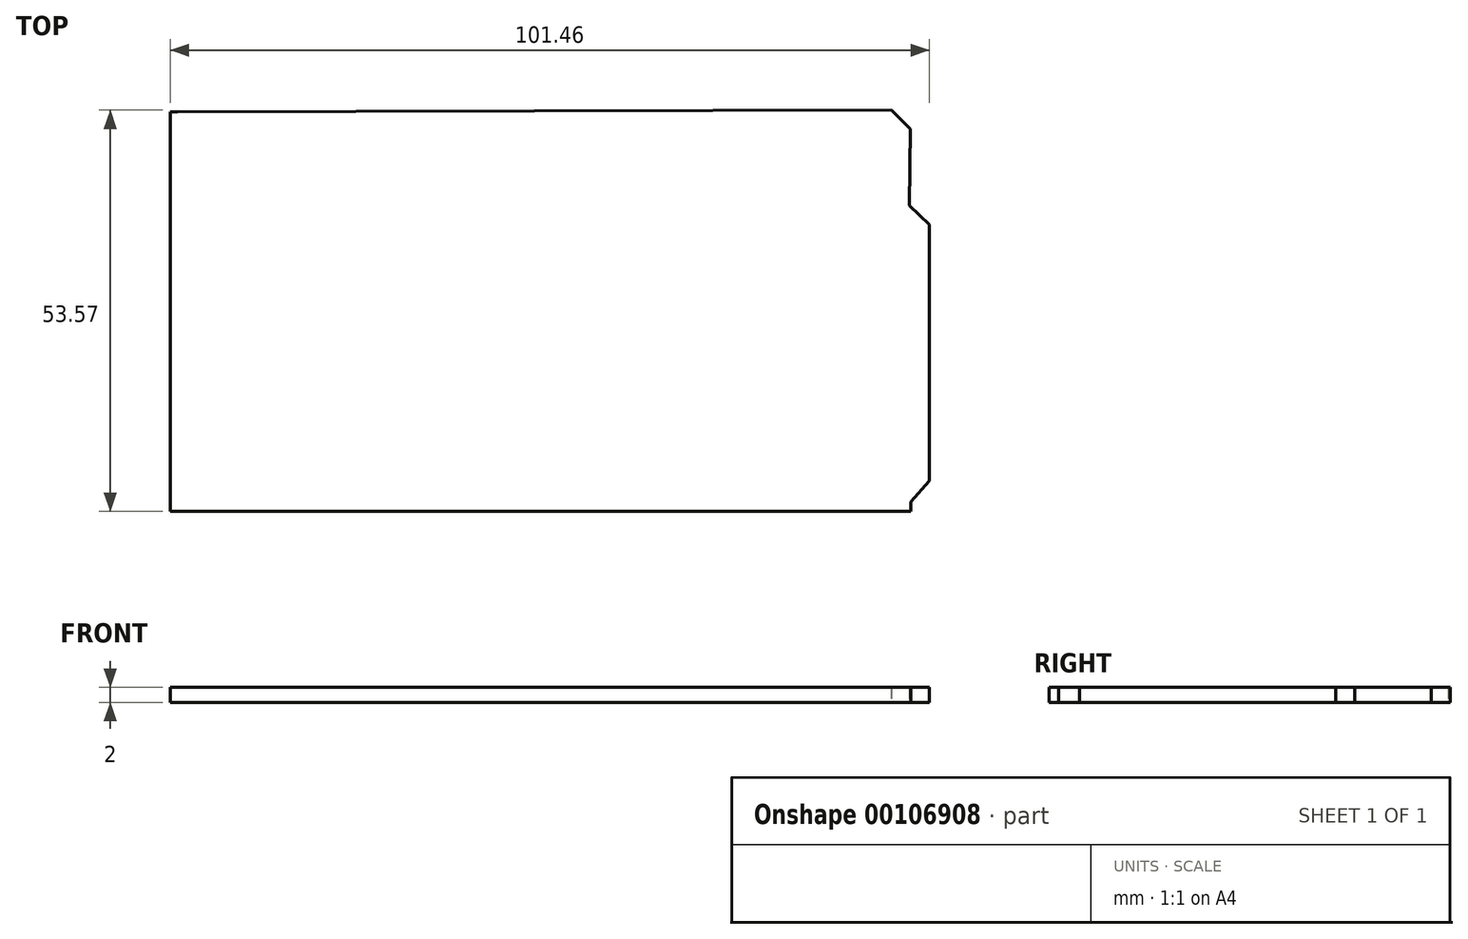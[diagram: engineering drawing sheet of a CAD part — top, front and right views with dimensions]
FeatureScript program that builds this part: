
annotation { "Feature Type Name" : "Feature", "Feature Type Description" : "" }
export const myFeature = defineFeature(function(context is Context, id is Id, definition is map)
    precondition{}
    {
        {
            var Q0;
            Q0=qCreatedBy(makeId("Top.planeOp"),FACE);
            var sketch = newSketch(context, id + "F0", { "sketchPlane" : qUnion([Q0])});
            skLineSegment(sketch, "E0", {"start": v(-9.69, 13.35) * mm, "end": v(-9.69, 13.4) * mm});
            skLineSegment(sketch, "E1", {"start": v(-9.69, 13.4) * mm, "end": v(-9.7, 13.46) * mm});
            skLineSegment(sketch, "E2", {"start": v(-9.7, 13.46) * mm, "end": v(-9.7, 13.51) * mm});
            skLineSegment(sketch, "E3", {"start": v(-9.7, 13.51) * mm, "end": v(-9.7, 13.57) * mm});
            skLineSegment(sketch, "E4", {"start": v(-9.7, 13.57) * mm, "end": v(-9.71, 13.63) * mm});
            skLineSegment(sketch, "E5", {"start": v(-9.71, 13.63) * mm, "end": v(-9.72, 13.68) * mm});
            skLineSegment(sketch, "E6", {"start": v(-9.72, 13.68) * mm, "end": v(-9.73, 13.73) * mm});
            skLineSegment(sketch, "E7", {"start": v(-9.73, 13.73) * mm, "end": v(-9.75, 13.79) * mm});
            skLineSegment(sketch, "E8", {"start": v(-9.75, 13.79) * mm, "end": v(-9.76, 13.84) * mm});
            skLineSegment(sketch, "E9", {"start": v(-9.76, 13.84) * mm, "end": v(-9.78, 13.9) * mm});
            skLineSegment(sketch, "E10", {"start": v(-9.78, 13.9) * mm, "end": v(-9.8, 13.95) * mm});
            skLineSegment(sketch, "E11", {"start": v(-9.8, 13.95) * mm, "end": v(-9.82, 14) * mm});
            skLineSegment(sketch, "E12", {"start": v(-9.82, 14) * mm, "end": v(-9.85, 14.05) * mm});
            skLineSegment(sketch, "E13", {"start": v(-9.85, 14.05) * mm, "end": v(-9.87, 14.1) * mm});
            skLineSegment(sketch, "E14", {"start": v(-9.87, 14.1) * mm, "end": v(-9.9, 14.15) * mm});
            skLineSegment(sketch, "E15", {"start": v(-9.9, 14.15) * mm, "end": v(-9.93, 14.2) * mm});
            skLineSegment(sketch, "E16", {"start": v(-9.93, 14.2) * mm, "end": v(-9.96, 14.24) * mm});
            skLineSegment(sketch, "E17", {"start": v(-9.96, 14.24) * mm, "end": v(-9.99, 14.29) * mm});
            skLineSegment(sketch, "E18", {"start": v(-9.99, 14.29) * mm, "end": v(-10.02, 14.33) * mm});
            skLineSegment(sketch, "E19", {"start": v(-10.02, 14.33) * mm, "end": v(-10.06, 14.38) * mm});
            skLineSegment(sketch, "E20", {"start": v(-10.06, 14.38) * mm, "end": v(-10.1, 14.42) * mm});
            skLineSegment(sketch, "E21", {"start": v(-10.1, 14.42) * mm, "end": v(-10.13, 14.46) * mm});
            skLineSegment(sketch, "E22", {"start": v(-10.13, 14.46) * mm, "end": v(-10.17, 14.5) * mm});
            skLineSegment(sketch, "E23", {"start": v(-10.17, 14.5) * mm, "end": v(-10.21, 14.54) * mm});
            skLineSegment(sketch, "E24", {"start": v(-10.21, 14.54) * mm, "end": v(-10.25, 14.57) * mm});
            skLineSegment(sketch, "E25", {"start": v(-10.25, 14.57) * mm, "end": v(-10.3, 14.6) * mm});
            skLineSegment(sketch, "E26", {"start": v(-10.3, 14.6) * mm, "end": v(-10.34, 14.64) * mm});
            skLineSegment(sketch, "E27", {"start": v(-10.34, 14.64) * mm, "end": v(-10.39, 14.67) * mm});
            skLineSegment(sketch, "E28", {"start": v(-10.39, 14.67) * mm, "end": v(-10.43, 14.7) * mm});
            skLineSegment(sketch, "E29", {"start": v(-10.43, 14.7) * mm, "end": v(-10.48, 14.73) * mm});
            skLineSegment(sketch, "E30", {"start": v(-10.48, 14.73) * mm, "end": v(-10.53, 14.76) * mm});
            skLineSegment(sketch, "E31", {"start": v(-10.53, 14.76) * mm, "end": v(-10.58, 14.79) * mm});
            skLineSegment(sketch, "E32", {"start": v(-10.58, 14.79) * mm, "end": v(-10.63, 14.81) * mm});
            skLineSegment(sketch, "E33", {"start": v(-10.63, 14.81) * mm, "end": v(-10.68, 14.83) * mm});
            skLineSegment(sketch, "E34", {"start": v(-10.68, 14.83) * mm, "end": v(-10.73, 14.85) * mm});
            skLineSegment(sketch, "E35", {"start": v(-10.73, 14.85) * mm, "end": v(-10.78, 14.87) * mm});
            skLineSegment(sketch, "E36", {"start": v(-10.78, 14.87) * mm, "end": v(-10.84, 14.89) * mm});
            skLineSegment(sketch, "E37", {"start": v(-10.84, 14.89) * mm, "end": v(-10.9, 14.9) * mm});
            skLineSegment(sketch, "E38", {"start": v(-10.9, 14.9) * mm, "end": v(-10.95, 14.92) * mm});
            skLineSegment(sketch, "E39", {"start": v(-10.95, 14.92) * mm, "end": v(-11, 14.93) * mm});
            skLineSegment(sketch, "E40", {"start": v(-11, 14.93) * mm, "end": v(-11.05, 14.94) * mm});
            skLineSegment(sketch, "E41", {"start": v(-11.05, 14.94) * mm, "end": v(-11.1, 14.95) * mm});
            skLineSegment(sketch, "E42", {"start": v(-11.1, 14.95) * mm, "end": v(-11.17, 14.95) * mm});
            skLineSegment(sketch, "E43", {"start": v(-11.17, 14.95) * mm, "end": v(-11.22, 14.95) * mm});
            skLineSegment(sketch, "E44", {"start": v(-11.22, 14.95) * mm, "end": v(-11.28, 14.96) * mm});
            skLineSegment(sketch, "E45", {"start": v(-11.28, 14.96) * mm, "end": v(-11.33, 14.96) * mm});
            skLineSegment(sketch, "E46", {"start": v(-11.33, 14.96) * mm, "end": v(-11.39, 14.95) * mm});
            skLineSegment(sketch, "E47", {"start": v(-11.39, 14.95) * mm, "end": v(-11.44, 14.95) * mm});
            skLineSegment(sketch, "E48", {"start": v(-11.44, 14.95) * mm, "end": v(-11.5, 14.94) * mm});
            skLineSegment(sketch, "E49", {"start": v(-11.5, 14.94) * mm, "end": v(-11.55, 14.94) * mm});
            skLineSegment(sketch, "E50", {"start": v(-11.55, 14.94) * mm, "end": v(-11.6, 14.93) * mm});
            skLineSegment(sketch, "E51", {"start": v(-11.6, 14.93) * mm, "end": v(-11.66, 14.91) * mm});
            skLineSegment(sketch, "E52", {"start": v(-11.66, 14.91) * mm, "end": v(-11.72, 14.9) * mm});
            skLineSegment(sketch, "E53", {"start": v(-11.72, 14.9) * mm, "end": v(-11.77, 14.88) * mm});
            skLineSegment(sketch, "E54", {"start": v(-11.77, 14.88) * mm, "end": v(-11.82, 14.87) * mm});
            skLineSegment(sketch, "E55", {"start": v(-11.82, 14.87) * mm, "end": v(-11.88, 14.85) * mm});
            skLineSegment(sketch, "E56", {"start": v(-11.88, 14.85) * mm, "end": v(-11.93, 14.83) * mm});
            skLineSegment(sketch, "E57", {"start": v(-11.93, 14.83) * mm, "end": v(-11.98, 14.8) * mm});
            skLineSegment(sketch, "E58", {"start": v(-11.98, 14.8) * mm, "end": v(-12.03, 14.78) * mm});
            skLineSegment(sketch, "E59", {"start": v(-12.03, 14.78) * mm, "end": v(-12.08, 14.75) * mm});
            skLineSegment(sketch, "E60", {"start": v(-12.08, 14.75) * mm, "end": v(-12.13, 14.72) * mm});
            skLineSegment(sketch, "E61", {"start": v(-12.13, 14.72) * mm, "end": v(-12.17, 14.7) * mm});
            skLineSegment(sketch, "E62", {"start": v(-12.17, 14.7) * mm, "end": v(-12.22, 14.66) * mm});
            skLineSegment(sketch, "E63", {"start": v(-12.22, 14.66) * mm, "end": v(-12.26, 14.63) * mm});
            skLineSegment(sketch, "E64", {"start": v(-12.26, 14.63) * mm, "end": v(-12.3, 14.6) * mm});
            skLineSegment(sketch, "E65", {"start": v(-12.3, 14.6) * mm, "end": v(-12.35, 14.56) * mm});
            skLineSegment(sketch, "E66", {"start": v(-12.35, 14.56) * mm, "end": v(-12.4, 14.52) * mm});
            skLineSegment(sketch, "E67", {"start": v(-12.4, 14.52) * mm, "end": v(-12.43, 14.49) * mm});
            skLineSegment(sketch, "E68", {"start": v(-12.43, 14.49) * mm, "end": v(-12.47, 14.45) * mm});
            skLineSegment(sketch, "E69", {"start": v(-12.47, 14.45) * mm, "end": v(-12.5, 14.4) * mm});
            skLineSegment(sketch, "E70", {"start": v(-12.5, 14.4) * mm, "end": v(-12.54, 14.36) * mm});
            skLineSegment(sketch, "E71", {"start": v(-12.54, 14.36) * mm, "end": v(-12.58, 14.32) * mm});
            skLineSegment(sketch, "E72", {"start": v(-12.58, 14.32) * mm, "end": v(-12.61, 14.27) * mm});
            skLineSegment(sketch, "E73", {"start": v(-12.61, 14.27) * mm, "end": v(-12.64, 14.23) * mm});
            skLineSegment(sketch, "E74", {"start": v(-12.64, 14.23) * mm, "end": v(-12.67, 14.18) * mm});
            skLineSegment(sketch, "E75", {"start": v(-12.67, 14.18) * mm, "end": v(-12.7, 14.13) * mm});
            skLineSegment(sketch, "E76", {"start": v(-12.7, 14.13) * mm, "end": v(-12.73, 14.08) * mm});
            skLineSegment(sketch, "E77", {"start": v(-12.73, 14.08) * mm, "end": v(-12.75, 14.03) * mm});
            skLineSegment(sketch, "E78", {"start": v(-12.75, 14.03) * mm, "end": v(-12.77, 13.98) * mm});
            skLineSegment(sketch, "E79", {"start": v(-12.77, 13.98) * mm, "end": v(-12.8, 13.93) * mm});
            skLineSegment(sketch, "E80", {"start": v(-12.8, 13.93) * mm, "end": v(-12.81, 13.88) * mm});
            skLineSegment(sketch, "E81", {"start": v(-12.81, 13.88) * mm, "end": v(-12.83, 13.82) * mm});
            skLineSegment(sketch, "E82", {"start": v(-12.83, 13.82) * mm, "end": v(-12.85, 13.77) * mm});
            skLineSegment(sketch, "E83", {"start": v(-12.85, 13.77) * mm, "end": v(-12.86, 13.72) * mm});
            skLineSegment(sketch, "E84", {"start": v(-12.86, 13.72) * mm, "end": v(-12.87, 13.66) * mm});
            skLineSegment(sketch, "E85", {"start": v(-12.87, 13.66) * mm, "end": v(-12.88, 13.6) * mm});
            skLineSegment(sketch, "E86", {"start": v(-12.88, 13.6) * mm, "end": v(-12.9, 13.55) * mm});
            skLineSegment(sketch, "E87", {"start": v(-12.9, 13.55) * mm, "end": v(-12.9, 13.5) * mm});
            skLineSegment(sketch, "E88", {"start": v(-12.9, 13.5) * mm, "end": v(-12.9, 13.44) * mm});
            skLineSegment(sketch, "E89", {"start": v(-12.9, 13.44) * mm, "end": v(-12.9, 13.39) * mm});
            skLineSegment(sketch, "E90", {"start": v(-12.9, 13.39) * mm, "end": v(-12.9, 13.33) * mm});
            skLineSegment(sketch, "E91", {"start": v(-12.9, 13.33) * mm, "end": v(-12.9, 13.27) * mm});
            skLineSegment(sketch, "E92", {"start": v(-12.9, 13.27) * mm, "end": v(-12.9, 13.22) * mm});
            skLineSegment(sketch, "E93", {"start": v(-12.9, 13.22) * mm, "end": v(-12.9, 13.16) * mm});
            skLineSegment(sketch, "E94", {"start": v(-12.9, 13.16) * mm, "end": v(-12.89, 13.1) * mm});
            skLineSegment(sketch, "E95", {"start": v(-12.89, 13.1) * mm, "end": v(-12.88, 13.05) * mm});
            skLineSegment(sketch, "E96", {"start": v(-12.88, 13.05) * mm, "end": v(-12.86, 13) * mm});
            skLineSegment(sketch, "E97", {"start": v(-12.86, 13) * mm, "end": v(-12.85, 12.94) * mm});
            skLineSegment(sketch, "E98", {"start": v(-12.85, 12.94) * mm, "end": v(-12.84, 12.9) * mm});
            skLineSegment(sketch, "E99", {"start": v(-12.84, 12.9) * mm, "end": v(-12.82, 12.84) * mm});
            skLineSegment(sketch, "E100", {"start": v(-12.82, 12.84) * mm, "end": v(-12.8, 12.78) * mm});
            skLineSegment(sketch, "E101", {"start": v(-12.8, 12.78) * mm, "end": v(-12.78, 12.73) * mm});
            skLineSegment(sketch, "E102", {"start": v(-12.78, 12.73) * mm, "end": v(-12.76, 12.68) * mm});
            skLineSegment(sketch, "E103", {"start": v(-12.76, 12.68) * mm, "end": v(-12.73, 12.63) * mm});
            skLineSegment(sketch, "E104", {"start": v(-12.73, 12.63) * mm, "end": v(-12.7, 12.58) * mm});
            skLineSegment(sketch, "E105", {"start": v(-12.7, 12.58) * mm, "end": v(-12.68, 12.53) * mm});
            skLineSegment(sketch, "E106", {"start": v(-12.68, 12.53) * mm, "end": v(-12.65, 12.49) * mm});
            skLineSegment(sketch, "E107", {"start": v(-12.65, 12.49) * mm, "end": v(-12.62, 12.44) * mm});
            skLineSegment(sketch, "E108", {"start": v(-12.62, 12.44) * mm, "end": v(-12.59, 12.4) * mm});
            skLineSegment(sketch, "E109", {"start": v(-12.59, 12.4) * mm, "end": v(-12.56, 12.35) * mm});
            skLineSegment(sketch, "E110", {"start": v(-12.56, 12.35) * mm, "end": v(-12.52, 12.3) * mm});
            skLineSegment(sketch, "E111", {"start": v(-12.52, 12.3) * mm, "end": v(-12.48, 12.26) * mm});
            skLineSegment(sketch, "E112", {"start": v(-12.48, 12.26) * mm, "end": v(-12.45, 12.22) * mm});
            skLineSegment(sketch, "E113", {"start": v(-12.45, 12.22) * mm, "end": v(-12.4, 12.18) * mm});
            skLineSegment(sketch, "E114", {"start": v(-12.4, 12.18) * mm, "end": v(-12.36, 12.15) * mm});
            skLineSegment(sketch, "E115", {"start": v(-12.36, 12.15) * mm, "end": v(-12.32, 12.11) * mm});
            skLineSegment(sketch, "E116", {"start": v(-12.32, 12.11) * mm, "end": v(-12.28, 12.08) * mm});
            skLineSegment(sketch, "E117", {"start": v(-12.28, 12.08) * mm, "end": v(-12.23, 12.04) * mm});
            skLineSegment(sketch, "E118", {"start": v(-12.23, 12.04) * mm, "end": v(-12.19, 12.01) * mm});
            skLineSegment(sketch, "E119", {"start": v(-12.19, 12.01) * mm, "end": v(-12.14, 11.98) * mm});
            skLineSegment(sketch, "E120", {"start": v(-12.14, 11.98) * mm, "end": v(-12.1, 11.95) * mm});
            skLineSegment(sketch, "E121", {"start": v(-12.1, 11.95) * mm, "end": v(-12.05, 11.93) * mm});
            skLineSegment(sketch, "E122", {"start": v(-12.05, 11.93) * mm, "end": v(-12, 11.9) * mm});
            skLineSegment(sketch, "E123", {"start": v(-12, 11.9) * mm, "end": v(-11.94, 11.88) * mm});
            skLineSegment(sketch, "E124", {"start": v(-11.94, 11.88) * mm, "end": v(-11.9, 11.86) * mm});
            skLineSegment(sketch, "E125", {"start": v(-11.9, 11.86) * mm, "end": v(-11.84, 11.84) * mm});
            skLineSegment(sketch, "E126", {"start": v(-11.84, 11.84) * mm, "end": v(-11.79, 11.82) * mm});
            skLineSegment(sketch, "E127", {"start": v(-11.79, 11.82) * mm, "end": v(-11.74, 11.8) * mm});
            skLineSegment(sketch, "E128", {"start": v(-11.74, 11.8) * mm, "end": v(-11.68, 11.79) * mm});
            skLineSegment(sketch, "E129", {"start": v(-11.68, 11.79) * mm, "end": v(-11.63, 11.77) * mm});
            skLineSegment(sketch, "E130", {"start": v(-11.63, 11.77) * mm, "end": v(-11.57, 11.76) * mm});
            skLineSegment(sketch, "E131", {"start": v(-11.57, 11.76) * mm, "end": v(-11.52, 11.76) * mm});
            skLineSegment(sketch, "E132", {"start": v(-11.52, 11.76) * mm, "end": v(-11.46, 11.75) * mm});
            skLineSegment(sketch, "E133", {"start": v(-11.46, 11.75) * mm, "end": v(-11.4, 11.74) * mm});
            skLineSegment(sketch, "E134", {"start": v(-11.4, 11.74) * mm, "end": v(-11.35, 11.74) * mm});
            skLineSegment(sketch, "E135", {"start": v(-11.35, 11.74) * mm, "end": v(-11.3, 11.74) * mm});
            skLineSegment(sketch, "E136", {"start": v(-11.3, 11.74) * mm, "end": v(-11.24, 11.74) * mm});
            skLineSegment(sketch, "E137", {"start": v(-11.24, 11.74) * mm, "end": v(-11.18, 11.74) * mm});
            skLineSegment(sketch, "E138", {"start": v(-11.18, 11.74) * mm, "end": v(-11.13, 11.75) * mm});
            skLineSegment(sketch, "E139", {"start": v(-11.13, 11.75) * mm, "end": v(-11.07, 11.76) * mm});
            skLineSegment(sketch, "E140", {"start": v(-11.07, 11.76) * mm, "end": v(-11.02, 11.76) * mm});
            skLineSegment(sketch, "E141", {"start": v(-11.02, 11.76) * mm, "end": v(-10.96, 11.78) * mm});
            skLineSegment(sketch, "E142", {"start": v(-10.96, 11.78) * mm, "end": v(-10.9, 11.79) * mm});
            skLineSegment(sketch, "E143", {"start": v(-10.9, 11.79) * mm, "end": v(-10.85, 11.8) * mm});
            skLineSegment(sketch, "E144", {"start": v(-10.85, 11.8) * mm, "end": v(-10.8, 11.82) * mm});
            skLineSegment(sketch, "E145", {"start": v(-10.8, 11.82) * mm, "end": v(-10.75, 11.84) * mm});
            skLineSegment(sketch, "E146", {"start": v(-10.75, 11.84) * mm, "end": v(-10.7, 11.86) * mm});
            skLineSegment(sketch, "E147", {"start": v(-10.7, 11.86) * mm, "end": v(-10.64, 11.88) * mm});
            skLineSegment(sketch, "E148", {"start": v(-10.64, 11.88) * mm, "end": v(-10.6, 11.9) * mm});
            skLineSegment(sketch, "E149", {"start": v(-10.6, 11.9) * mm, "end": v(-10.54, 11.93) * mm});
            skLineSegment(sketch, "E150", {"start": v(-10.54, 11.93) * mm, "end": v(-10.5, 11.96) * mm});
            skLineSegment(sketch, "E151", {"start": v(-10.5, 11.96) * mm, "end": v(-10.44, 11.98) * mm});
            skLineSegment(sketch, "E152", {"start": v(-10.44, 11.98) * mm, "end": v(-10.4, 12.01) * mm});
            skLineSegment(sketch, "E153", {"start": v(-10.4, 12.01) * mm, "end": v(-10.35, 12.05) * mm});
            skLineSegment(sketch, "E154", {"start": v(-10.35, 12.05) * mm, "end": v(-10.3, 12.08) * mm});
            skLineSegment(sketch, "E155", {"start": v(-10.3, 12.08) * mm, "end": v(-10.26, 12.12) * mm});
            skLineSegment(sketch, "E156", {"start": v(-10.26, 12.12) * mm, "end": v(-10.22, 12.15) * mm});
            skLineSegment(sketch, "E157", {"start": v(-10.22, 12.15) * mm, "end": v(-10.18, 12.2) * mm});
            skLineSegment(sketch, "E158", {"start": v(-10.18, 12.2) * mm, "end": v(-10.14, 12.23) * mm});
            skLineSegment(sketch, "E159", {"start": v(-10.14, 12.23) * mm, "end": v(-10.1, 12.27) * mm});
            skLineSegment(sketch, "E160", {"start": v(-10.1, 12.27) * mm, "end": v(-10.06, 12.31) * mm});
            skLineSegment(sketch, "E161", {"start": v(-10.06, 12.31) * mm, "end": v(-10.03, 12.36) * mm});
            skLineSegment(sketch, "E162", {"start": v(-10.03, 12.36) * mm, "end": v(-10, 12.4) * mm});
            skLineSegment(sketch, "E163", {"start": v(-10, 12.4) * mm, "end": v(-9.96, 12.45) * mm});
            skLineSegment(sketch, "E164", {"start": v(-9.96, 12.45) * mm, "end": v(-9.93, 12.5) * mm});
            skLineSegment(sketch, "E165", {"start": v(-9.93, 12.5) * mm, "end": v(-9.9, 12.54) * mm});
            skLineSegment(sketch, "E166", {"start": v(-9.9, 12.54) * mm, "end": v(-9.88, 12.6) * mm});
            skLineSegment(sketch, "E167", {"start": v(-9.88, 12.6) * mm, "end": v(-9.85, 12.64) * mm});
            skLineSegment(sketch, "E168", {"start": v(-9.85, 12.64) * mm, "end": v(-9.83, 12.7) * mm});
            skLineSegment(sketch, "E169", {"start": v(-9.83, 12.7) * mm, "end": v(-9.8, 12.75) * mm});
            skLineSegment(sketch, "E170", {"start": v(-9.8, 12.75) * mm, "end": v(-9.78, 12.8) * mm});
            skLineSegment(sketch, "E171", {"start": v(-9.78, 12.8) * mm, "end": v(-9.77, 12.85) * mm});
            skLineSegment(sketch, "E172", {"start": v(-9.77, 12.85) * mm, "end": v(-9.75, 12.9) * mm});
            skLineSegment(sketch, "E173", {"start": v(-9.75, 12.9) * mm, "end": v(-9.73, 12.96) * mm});
            skLineSegment(sketch, "E174", {"start": v(-9.73, 12.96) * mm, "end": v(-9.72, 13.01) * mm});
            skLineSegment(sketch, "E175", {"start": v(-9.72, 13.01) * mm, "end": v(-9.71, 13.07) * mm});
            skLineSegment(sketch, "E176", {"start": v(-9.71, 13.07) * mm, "end": v(-9.7, 13.12) * mm});
            skLineSegment(sketch, "E177", {"start": v(-9.7, 13.12) * mm, "end": v(-9.7, 13.18) * mm});
            skLineSegment(sketch, "E178", {"start": v(-9.7, 13.18) * mm, "end": v(-9.7, 13.24) * mm});
            skLineSegment(sketch, "E179", {"start": v(-9.7, 13.24) * mm, "end": v(-9.69, 13.3) * mm});
            skLineSegment(sketch, "E180", {"start": v(-9.69, 13.3) * mm, "end": v(-9.69, 13.35) * mm});
            skLineSegment(sketch, "E181", {"start": v(14.43, 28.58) * mm, "end": v(14.43, 28.64) * mm});
            skLineSegment(sketch, "E182", {"start": v(14.43, 28.64) * mm, "end": v(14.43, 28.7) * mm});
            skLineSegment(sketch, "E183", {"start": v(14.43, 28.7) * mm, "end": v(14.43, 28.75) * mm});
            skLineSegment(sketch, "E184", {"start": v(14.43, 28.75) * mm, "end": v(14.42, 28.8) * mm});
            skLineSegment(sketch, "E185", {"start": v(14.42, 28.8) * mm, "end": v(14.41, 28.86) * mm});
            skLineSegment(sketch, "E186", {"start": v(14.41, 28.86) * mm, "end": v(14.4, 28.91) * mm});
            skLineSegment(sketch, "E187", {"start": v(14.4, 28.91) * mm, "end": v(14.39, 28.97) * mm});
            skLineSegment(sketch, "E188", {"start": v(14.39, 28.97) * mm, "end": v(14.37, 29.02) * mm});
            skLineSegment(sketch, "E189", {"start": v(14.37, 29.02) * mm, "end": v(14.36, 29.08) * mm});
            skLineSegment(sketch, "E190", {"start": v(14.36, 29.08) * mm, "end": v(14.34, 29.13) * mm});
            skLineSegment(sketch, "E191", {"start": v(14.34, 29.13) * mm, "end": v(14.32, 29.18) * mm});
            skLineSegment(sketch, "E192", {"start": v(14.32, 29.18) * mm, "end": v(14.3, 29.23) * mm});
            skLineSegment(sketch, "E193", {"start": v(14.3, 29.23) * mm, "end": v(14.27, 29.28) * mm});
            skLineSegment(sketch, "E194", {"start": v(14.27, 29.28) * mm, "end": v(14.25, 29.33) * mm});
            skLineSegment(sketch, "E195", {"start": v(14.25, 29.33) * mm, "end": v(14.22, 29.38) * mm});
            skLineSegment(sketch, "E196", {"start": v(14.22, 29.38) * mm, "end": v(14.2, 29.43) * mm});
            skLineSegment(sketch, "E197", {"start": v(14.2, 29.43) * mm, "end": v(14.16, 29.48) * mm});
            skLineSegment(sketch, "E198", {"start": v(14.16, 29.48) * mm, "end": v(14.13, 29.52) * mm});
            skLineSegment(sketch, "E199", {"start": v(14.13, 29.52) * mm, "end": v(14.1, 29.57) * mm});
            skLineSegment(sketch, "E200", {"start": v(14.1, 29.57) * mm, "end": v(14.06, 29.6) * mm});
            skLineSegment(sketch, "E201", {"start": v(14.06, 29.6) * mm, "end": v(14.03, 29.65) * mm});
            skLineSegment(sketch, "E202", {"start": v(14.03, 29.65) * mm, "end": v(13.99, 29.7) * mm});
            skLineSegment(sketch, "E203", {"start": v(13.99, 29.7) * mm, "end": v(13.95, 29.73) * mm});
            skLineSegment(sketch, "E204", {"start": v(13.95, 29.73) * mm, "end": v(13.9, 29.77) * mm});
            skLineSegment(sketch, "E205", {"start": v(13.9, 29.77) * mm, "end": v(13.87, 29.8) * mm});
            skLineSegment(sketch, "E206", {"start": v(13.87, 29.8) * mm, "end": v(13.82, 29.84) * mm});
            skLineSegment(sketch, "E207", {"start": v(13.82, 29.84) * mm, "end": v(13.78, 29.88) * mm});
            skLineSegment(sketch, "E208", {"start": v(13.78, 29.88) * mm, "end": v(13.74, 29.9) * mm});
            skLineSegment(sketch, "E209", {"start": v(13.74, 29.9) * mm, "end": v(13.69, 29.94) * mm});
            skLineSegment(sketch, "E210", {"start": v(13.69, 29.94) * mm, "end": v(13.64, 29.97) * mm});
            skLineSegment(sketch, "E211", {"start": v(13.64, 29.97) * mm, "end": v(13.6, 30) * mm});
            skLineSegment(sketch, "E212", {"start": v(13.6, 30) * mm, "end": v(13.54, 30.02) * mm});
            skLineSegment(sketch, "E213", {"start": v(13.54, 30.02) * mm, "end": v(13.5, 30.05) * mm});
            skLineSegment(sketch, "E214", {"start": v(13.5, 30.05) * mm, "end": v(13.44, 30.07) * mm});
            skLineSegment(sketch, "E215", {"start": v(13.44, 30.07) * mm, "end": v(13.39, 30.09) * mm});
            skLineSegment(sketch, "E216", {"start": v(13.39, 30.09) * mm, "end": v(13.34, 30.1) * mm});
            skLineSegment(sketch, "E217", {"start": v(13.34, 30.1) * mm, "end": v(13.28, 30.12) * mm});
            skLineSegment(sketch, "E218", {"start": v(13.28, 30.12) * mm, "end": v(13.23, 30.14) * mm});
            skLineSegment(sketch, "E219", {"start": v(13.23, 30.14) * mm, "end": v(13.18, 30.15) * mm});
            skLineSegment(sketch, "E220", {"start": v(13.18, 30.15) * mm, "end": v(13.12, 30.16) * mm});
            skLineSegment(sketch, "E221", {"start": v(13.12, 30.16) * mm, "end": v(13.07, 30.17) * mm});
            skLineSegment(sketch, "E222", {"start": v(13.07, 30.17) * mm, "end": v(13.01, 30.18) * mm});
            skLineSegment(sketch, "E223", {"start": v(13.01, 30.18) * mm, "end": v(12.96, 30.19) * mm});
            skLineSegment(sketch, "E224", {"start": v(12.96, 30.19) * mm, "end": v(12.9, 30.19) * mm});
            skLineSegment(sketch, "E225", {"start": v(12.9, 30.19) * mm, "end": v(12.84, 30.2) * mm});
            skLineSegment(sketch, "E226", {"start": v(12.84, 30.2) * mm, "end": v(12.79, 30.2) * mm});
            skLineSegment(sketch, "E227", {"start": v(12.79, 30.2) * mm, "end": v(12.73, 30.19) * mm});
            skLineSegment(sketch, "E228", {"start": v(12.73, 30.19) * mm, "end": v(12.68, 30.18) * mm});
            skLineSegment(sketch, "E229", {"start": v(12.68, 30.18) * mm, "end": v(12.62, 30.18) * mm});
            skLineSegment(sketch, "E230", {"start": v(12.62, 30.18) * mm, "end": v(12.57, 30.17) * mm});
            skLineSegment(sketch, "E231", {"start": v(12.57, 30.17) * mm, "end": v(12.51, 30.16) * mm});
            skLineSegment(sketch, "E232", {"start": v(12.51, 30.16) * mm, "end": v(12.46, 30.15) * mm});
            skLineSegment(sketch, "E233", {"start": v(12.46, 30.15) * mm, "end": v(12.4, 30.13) * mm});
            skLineSegment(sketch, "E234", {"start": v(12.4, 30.13) * mm, "end": v(12.35, 30.12) * mm});
            skLineSegment(sketch, "E235", {"start": v(12.35, 30.12) * mm, "end": v(12.3, 30.1) * mm});
            skLineSegment(sketch, "E236", {"start": v(12.3, 30.1) * mm, "end": v(12.25, 30.08) * mm});
            skLineSegment(sketch, "E237", {"start": v(12.25, 30.08) * mm, "end": v(12.2, 30.06) * mm});
            skLineSegment(sketch, "E238", {"start": v(12.2, 30.06) * mm, "end": v(12.14, 30.04) * mm});
            skLineSegment(sketch, "E239", {"start": v(12.14, 30.04) * mm, "end": v(12.1, 30.01) * mm});
            skLineSegment(sketch, "E240", {"start": v(12.1, 30.01) * mm, "end": v(12.04, 29.99) * mm});
            skLineSegment(sketch, "E241", {"start": v(12.04, 29.99) * mm, "end": v(12, 29.96) * mm});
            skLineSegment(sketch, "E242", {"start": v(12, 29.96) * mm, "end": v(11.95, 29.93) * mm});
            skLineSegment(sketch, "E243", {"start": v(11.95, 29.93) * mm, "end": v(11.9, 29.9) * mm});
            skLineSegment(sketch, "E244", {"start": v(11.9, 29.9) * mm, "end": v(11.86, 29.87) * mm});
            skLineSegment(sketch, "E245", {"start": v(11.86, 29.87) * mm, "end": v(11.81, 29.83) * mm});
            skLineSegment(sketch, "E246", {"start": v(11.81, 29.83) * mm, "end": v(11.77, 29.8) * mm});
            skLineSegment(sketch, "E247", {"start": v(11.77, 29.8) * mm, "end": v(11.73, 29.76) * mm});
            skLineSegment(sketch, "E248", {"start": v(11.73, 29.76) * mm, "end": v(11.69, 29.72) * mm});
            skLineSegment(sketch, "E249", {"start": v(11.69, 29.72) * mm, "end": v(11.65, 29.68) * mm});
            skLineSegment(sketch, "E250", {"start": v(11.65, 29.68) * mm, "end": v(11.61, 29.64) * mm});
            skLineSegment(sketch, "E251", {"start": v(11.61, 29.64) * mm, "end": v(11.58, 29.6) * mm});
            skLineSegment(sketch, "E252", {"start": v(11.58, 29.6) * mm, "end": v(11.54, 29.55) * mm});
            skLineSegment(sketch, "E253", {"start": v(11.54, 29.55) * mm, "end": v(11.51, 29.5) * mm});
            skLineSegment(sketch, "E254", {"start": v(11.51, 29.5) * mm, "end": v(11.48, 29.46) * mm});
            skLineSegment(sketch, "E255", {"start": v(11.48, 29.46) * mm, "end": v(11.45, 29.41) * mm});
            skLineSegment(sketch, "E256", {"start": v(11.45, 29.41) * mm, "end": v(11.42, 29.37) * mm});
            skLineSegment(sketch, "E257", {"start": v(11.42, 29.37) * mm, "end": v(11.4, 29.32) * mm});
            skLineSegment(sketch, "E258", {"start": v(11.4, 29.32) * mm, "end": v(11.37, 29.27) * mm});
            skLineSegment(sketch, "E259", {"start": v(11.37, 29.27) * mm, "end": v(11.35, 29.22) * mm});
            skLineSegment(sketch, "E260", {"start": v(11.35, 29.22) * mm, "end": v(11.33, 29.16) * mm});
            skLineSegment(sketch, "E261", {"start": v(11.33, 29.16) * mm, "end": v(11.3, 29.11) * mm});
            skLineSegment(sketch, "E262", {"start": v(11.3, 29.11) * mm, "end": v(11.3, 29.06) * mm});
            skLineSegment(sketch, "E263", {"start": v(11.3, 29.06) * mm, "end": v(11.27, 29) * mm});
            skLineSegment(sketch, "E264", {"start": v(11.27, 29) * mm, "end": v(11.26, 28.95) * mm});
            skLineSegment(sketch, "E265", {"start": v(11.26, 28.95) * mm, "end": v(11.25, 28.9) * mm});
            skLineSegment(sketch, "E266", {"start": v(11.25, 28.9) * mm, "end": v(11.24, 28.84) * mm});
            skLineSegment(sketch, "E267", {"start": v(11.24, 28.84) * mm, "end": v(11.23, 28.79) * mm});
            skLineSegment(sketch, "E268", {"start": v(11.23, 28.79) * mm, "end": v(11.23, 28.73) * mm});
            skLineSegment(sketch, "E269", {"start": v(11.23, 28.73) * mm, "end": v(11.22, 28.68) * mm});
            skLineSegment(sketch, "E270", {"start": v(11.22, 28.68) * mm, "end": v(11.22, 28.62) * mm});
            skLineSegment(sketch, "E271", {"start": v(11.22, 28.62) * mm, "end": v(11.22, 28.56) * mm});
            skLineSegment(sketch, "E272", {"start": v(11.22, 28.56) * mm, "end": v(11.22, 28.5) * mm});
            skLineSegment(sketch, "E273", {"start": v(11.22, 28.5) * mm, "end": v(11.22, 28.45) * mm});
            skLineSegment(sketch, "E274", {"start": v(11.22, 28.45) * mm, "end": v(11.23, 28.4) * mm});
            skLineSegment(sketch, "E275", {"start": v(11.23, 28.4) * mm, "end": v(11.24, 28.34) * mm});
            skLineSegment(sketch, "E276", {"start": v(11.24, 28.34) * mm, "end": v(11.25, 28.29) * mm});
            skLineSegment(sketch, "E277", {"start": v(11.25, 28.29) * mm, "end": v(11.26, 28.23) * mm});
            skLineSegment(sketch, "E278", {"start": v(11.26, 28.23) * mm, "end": v(11.27, 28.18) * mm});
            skLineSegment(sketch, "E279", {"start": v(11.27, 28.18) * mm, "end": v(11.28, 28.12) * mm});
            skLineSegment(sketch, "E280", {"start": v(11.28, 28.12) * mm, "end": v(11.3, 28.07) * mm});
            skLineSegment(sketch, "E281", {"start": v(11.3, 28.07) * mm, "end": v(11.32, 28.02) * mm});
            skLineSegment(sketch, "E282", {"start": v(11.32, 28.02) * mm, "end": v(11.34, 27.97) * mm});
            skLineSegment(sketch, "E283", {"start": v(11.34, 27.97) * mm, "end": v(11.36, 27.92) * mm});
            skLineSegment(sketch, "E284", {"start": v(11.36, 27.92) * mm, "end": v(11.39, 27.87) * mm});
            skLineSegment(sketch, "E285", {"start": v(11.39, 27.87) * mm, "end": v(11.41, 27.82) * mm});
            skLineSegment(sketch, "E286", {"start": v(11.41, 27.82) * mm, "end": v(11.44, 27.77) * mm});
            skLineSegment(sketch, "E287", {"start": v(11.44, 27.77) * mm, "end": v(11.47, 27.72) * mm});
            skLineSegment(sketch, "E288", {"start": v(11.47, 27.72) * mm, "end": v(11.5, 27.67) * mm});
            skLineSegment(sketch, "E289", {"start": v(11.5, 27.67) * mm, "end": v(11.53, 27.63) * mm});
            skLineSegment(sketch, "E290", {"start": v(11.53, 27.63) * mm, "end": v(11.57, 27.58) * mm});
            skLineSegment(sketch, "E291", {"start": v(11.57, 27.58) * mm, "end": v(11.6, 27.54) * mm});
            skLineSegment(sketch, "E292", {"start": v(11.6, 27.54) * mm, "end": v(11.64, 27.5) * mm});
            skLineSegment(sketch, "E293", {"start": v(11.64, 27.5) * mm, "end": v(11.68, 27.46) * mm});
            skLineSegment(sketch, "E294", {"start": v(11.68, 27.46) * mm, "end": v(11.72, 27.42) * mm});
            skLineSegment(sketch, "E295", {"start": v(11.72, 27.42) * mm, "end": v(11.76, 27.38) * mm});
            skLineSegment(sketch, "E296", {"start": v(11.76, 27.38) * mm, "end": v(11.8, 27.35) * mm});
            skLineSegment(sketch, "E297", {"start": v(11.8, 27.35) * mm, "end": v(11.84, 27.31) * mm});
            skLineSegment(sketch, "E298", {"start": v(11.84, 27.31) * mm, "end": v(11.89, 27.28) * mm});
            skLineSegment(sketch, "E299", {"start": v(11.89, 27.28) * mm, "end": v(11.93, 27.25) * mm});
            skLineSegment(sketch, "E300", {"start": v(11.93, 27.25) * mm, "end": v(11.98, 27.22) * mm});
            skLineSegment(sketch, "E301", {"start": v(11.98, 27.22) * mm, "end": v(12.03, 27.19) * mm});
            skLineSegment(sketch, "E302", {"start": v(12.03, 27.19) * mm, "end": v(12.08, 27.16) * mm});
            skLineSegment(sketch, "E303", {"start": v(12.08, 27.16) * mm, "end": v(12.13, 27.13) * mm});
            skLineSegment(sketch, "E304", {"start": v(12.13, 27.13) * mm, "end": v(12.18, 27.11) * mm});
            skLineSegment(sketch, "E305", {"start": v(12.18, 27.11) * mm, "end": v(12.23, 27.09) * mm});
            skLineSegment(sketch, "E306", {"start": v(12.23, 27.09) * mm, "end": v(12.28, 27.07) * mm});
            skLineSegment(sketch, "E307", {"start": v(12.28, 27.07) * mm, "end": v(12.33, 27.05) * mm});
            skLineSegment(sketch, "E308", {"start": v(12.33, 27.05) * mm, "end": v(12.39, 27.04) * mm});
            skLineSegment(sketch, "E309", {"start": v(12.39, 27.04) * mm, "end": v(12.44, 27.02) * mm});
            skLineSegment(sketch, "E310", {"start": v(12.44, 27.02) * mm, "end": v(12.5, 27) * mm});
            skLineSegment(sketch, "E311", {"start": v(12.5, 27) * mm, "end": v(12.55, 27) * mm});
            skLineSegment(sketch, "E312", {"start": v(12.55, 27) * mm, "end": v(12.6, 26.99) * mm});
            skLineSegment(sketch, "E313", {"start": v(12.6, 26.99) * mm, "end": v(12.66, 26.98) * mm});
            skLineSegment(sketch, "E314", {"start": v(12.66, 26.98) * mm, "end": v(12.71, 26.98) * mm});
            skLineSegment(sketch, "E315", {"start": v(12.71, 26.98) * mm, "end": v(12.77, 26.98) * mm});
            skLineSegment(sketch, "E316", {"start": v(12.77, 26.98) * mm, "end": v(12.83, 26.97) * mm});
            skLineSegment(sketch, "E317", {"start": v(12.83, 26.97) * mm, "end": v(12.88, 26.98) * mm});
            skLineSegment(sketch, "E318", {"start": v(12.88, 26.98) * mm, "end": v(12.94, 26.98) * mm});
            skLineSegment(sketch, "E319", {"start": v(12.94, 26.98) * mm, "end": v(13, 26.98) * mm});
            skLineSegment(sketch, "E320", {"start": v(13, 26.98) * mm, "end": v(13.05, 27) * mm});
            skLineSegment(sketch, "E321", {"start": v(13.05, 27) * mm, "end": v(13.1, 27) * mm});
            skLineSegment(sketch, "E322", {"start": v(13.1, 27) * mm, "end": v(13.16, 27) * mm});
            skLineSegment(sketch, "E323", {"start": v(13.16, 27) * mm, "end": v(13.22, 27.02) * mm});
            skLineSegment(sketch, "E324", {"start": v(13.22, 27.02) * mm, "end": v(13.27, 27.04) * mm});
            skLineSegment(sketch, "E325", {"start": v(13.27, 27.04) * mm, "end": v(13.32, 27.05) * mm});
            skLineSegment(sketch, "E326", {"start": v(13.32, 27.05) * mm, "end": v(13.38, 27.07) * mm});
            skLineSegment(sketch, "E327", {"start": v(13.38, 27.07) * mm, "end": v(13.43, 27.1) * mm});
            skLineSegment(sketch, "E328", {"start": v(13.43, 27.1) * mm, "end": v(13.48, 27.11) * mm});
            skLineSegment(sketch, "E329", {"start": v(13.48, 27.11) * mm, "end": v(13.53, 27.14) * mm});
            skLineSegment(sketch, "E330", {"start": v(13.53, 27.14) * mm, "end": v(13.58, 27.16) * mm});
            skLineSegment(sketch, "E331", {"start": v(13.58, 27.16) * mm, "end": v(13.63, 27.19) * mm});
            skLineSegment(sketch, "E332", {"start": v(13.63, 27.19) * mm, "end": v(13.68, 27.22) * mm});
            skLineSegment(sketch, "E333", {"start": v(13.68, 27.22) * mm, "end": v(13.73, 27.25) * mm});
            skLineSegment(sketch, "E334", {"start": v(13.73, 27.25) * mm, "end": v(13.77, 27.28) * mm});
            skLineSegment(sketch, "E335", {"start": v(13.77, 27.28) * mm, "end": v(13.82, 27.32) * mm});
            skLineSegment(sketch, "E336", {"start": v(13.82, 27.32) * mm, "end": v(13.86, 27.35) * mm});
            skLineSegment(sketch, "E337", {"start": v(13.86, 27.35) * mm, "end": v(13.9, 27.39) * mm});
            skLineSegment(sketch, "E338", {"start": v(13.9, 27.39) * mm, "end": v(13.94, 27.43) * mm});
            skLineSegment(sketch, "E339", {"start": v(13.94, 27.43) * mm, "end": v(13.98, 27.47) * mm});
            skLineSegment(sketch, "E340", {"start": v(13.98, 27.47) * mm, "end": v(14.02, 27.5) * mm});
            skLineSegment(sketch, "E341", {"start": v(14.02, 27.5) * mm, "end": v(14.06, 27.55) * mm});
            skLineSegment(sketch, "E342", {"start": v(14.06, 27.55) * mm, "end": v(14.1, 27.6) * mm});
            skLineSegment(sketch, "E343", {"start": v(14.1, 27.6) * mm, "end": v(14.13, 27.64) * mm});
            skLineSegment(sketch, "E344", {"start": v(14.13, 27.64) * mm, "end": v(14.16, 27.68) * mm});
            skLineSegment(sketch, "E345", {"start": v(14.16, 27.68) * mm, "end": v(14.2, 27.73) * mm});
            skLineSegment(sketch, "E346", {"start": v(14.2, 27.73) * mm, "end": v(14.22, 27.78) * mm});
            skLineSegment(sketch, "E347", {"start": v(14.22, 27.78) * mm, "end": v(14.25, 27.83) * mm});
            skLineSegment(sketch, "E348", {"start": v(14.25, 27.83) * mm, "end": v(14.27, 27.88) * mm});
            skLineSegment(sketch, "E349", {"start": v(14.27, 27.88) * mm, "end": v(14.3, 27.93) * mm});
            skLineSegment(sketch, "E350", {"start": v(14.3, 27.93) * mm, "end": v(14.32, 27.98) * mm});
            skLineSegment(sketch, "E351", {"start": v(14.32, 27.98) * mm, "end": v(14.34, 28.03) * mm});
            skLineSegment(sketch, "E352", {"start": v(14.34, 28.03) * mm, "end": v(14.36, 28.09) * mm});
            skLineSegment(sketch, "E353", {"start": v(14.36, 28.09) * mm, "end": v(14.37, 28.14) * mm});
            skLineSegment(sketch, "E354", {"start": v(14.37, 28.14) * mm, "end": v(14.39, 28.2) * mm});
            skLineSegment(sketch, "E355", {"start": v(14.39, 28.2) * mm, "end": v(14.4, 28.25) * mm});
            skLineSegment(sketch, "E356", {"start": v(14.4, 28.25) * mm, "end": v(14.4, 28.3) * mm});
            skLineSegment(sketch, "E357", {"start": v(14.4, 28.3) * mm, "end": v(14.42, 28.36) * mm});
            skLineSegment(sketch, "E358", {"start": v(14.42, 28.36) * mm, "end": v(14.43, 28.41) * mm});
            skLineSegment(sketch, "E359", {"start": v(14.43, 28.41) * mm, "end": v(14.43, 28.47) * mm});
            skLineSegment(sketch, "E360", {"start": v(14.43, 28.47) * mm, "end": v(14.43, 28.53) * mm});
            skLineSegment(sketch, "E361", {"start": v(14.43, 28.53) * mm, "end": v(14.43, 28.58) * mm});
            skLineSegment(sketch, "E362", {"start": v(20.76, -19.64) * mm, "end": v(20.76, -19.58) * mm});
            skLineSegment(sketch, "E363", {"start": v(20.76, -19.58) * mm, "end": v(20.76, -19.53) * mm});
            skLineSegment(sketch, "E364", {"start": v(20.76, -19.53) * mm, "end": v(20.75, -19.47) * mm});
            skLineSegment(sketch, "E365", {"start": v(20.75, -19.47) * mm, "end": v(20.75, -19.42) * mm});
            skLineSegment(sketch, "E366", {"start": v(20.75, -19.42) * mm, "end": v(20.74, -19.36) * mm});
            skLineSegment(sketch, "E367", {"start": v(20.74, -19.36) * mm, "end": v(20.73, -19.3) * mm});
            skLineSegment(sketch, "E368", {"start": v(20.73, -19.3) * mm, "end": v(20.71, -19.25) * mm});
            skLineSegment(sketch, "E369", {"start": v(20.71, -19.25) * mm, "end": v(20.7, -19.2) * mm});
            skLineSegment(sketch, "E370", {"start": v(20.7, -19.2) * mm, "end": v(20.68, -19.15) * mm});
            skLineSegment(sketch, "E371", {"start": v(20.68, -19.15) * mm, "end": v(20.67, -19.1) * mm});
            skLineSegment(sketch, "E372", {"start": v(20.67, -19.1) * mm, "end": v(20.65, -19.04) * mm});
            skLineSegment(sketch, "E373", {"start": v(20.65, -19.04) * mm, "end": v(20.62, -18.99) * mm});
            skLineSegment(sketch, "E374", {"start": v(20.62, -18.99) * mm, "end": v(20.6, -18.94) * mm});
            skLineSegment(sketch, "E375", {"start": v(20.6, -18.94) * mm, "end": v(20.58, -18.89) * mm});
            skLineSegment(sketch, "E376", {"start": v(20.58, -18.89) * mm, "end": v(20.55, -18.84) * mm});
            skLineSegment(sketch, "E377", {"start": v(20.55, -18.84) * mm, "end": v(20.52, -18.8) * mm});
            skLineSegment(sketch, "E378", {"start": v(20.52, -18.8) * mm, "end": v(20.49, -18.75) * mm});
            skLineSegment(sketch, "E379", {"start": v(20.49, -18.75) * mm, "end": v(20.46, -18.7) * mm});
            skLineSegment(sketch, "E380", {"start": v(20.46, -18.7) * mm, "end": v(20.42, -18.66) * mm});
            skLineSegment(sketch, "E381", {"start": v(20.42, -18.66) * mm, "end": v(20.4, -18.61) * mm});
            skLineSegment(sketch, "E382", {"start": v(20.4, -18.61) * mm, "end": v(20.35, -18.57) * mm});
            skLineSegment(sketch, "E383", {"start": v(20.35, -18.57) * mm, "end": v(20.32, -18.53) * mm});
            skLineSegment(sketch, "E384", {"start": v(20.32, -18.53) * mm, "end": v(20.28, -18.49) * mm});
            skLineSegment(sketch, "E385", {"start": v(20.28, -18.49) * mm, "end": v(20.24, -18.45) * mm});
            skLineSegment(sketch, "E386", {"start": v(20.24, -18.45) * mm, "end": v(20.2, -18.41) * mm});
            skLineSegment(sketch, "E387", {"start": v(20.2, -18.41) * mm, "end": v(20.15, -18.38) * mm});
            skLineSegment(sketch, "E388", {"start": v(20.15, -18.38) * mm, "end": v(20.1, -18.34) * mm});
            skLineSegment(sketch, "E389", {"start": v(20.1, -18.34) * mm, "end": v(20.06, -18.31) * mm});
            skLineSegment(sketch, "E390", {"start": v(20.06, -18.31) * mm, "end": v(20.02, -18.28) * mm});
            skLineSegment(sketch, "E391", {"start": v(20.02, -18.28) * mm, "end": v(19.97, -18.25) * mm});
            skLineSegment(sketch, "E392", {"start": v(19.97, -18.25) * mm, "end": v(19.92, -18.23) * mm});
            skLineSegment(sketch, "E393", {"start": v(19.92, -18.23) * mm, "end": v(19.87, -18.2) * mm});
            skLineSegment(sketch, "E394", {"start": v(19.87, -18.2) * mm, "end": v(19.82, -18.18) * mm});
            skLineSegment(sketch, "E395", {"start": v(19.82, -18.18) * mm, "end": v(19.77, -18.15) * mm});
            skLineSegment(sketch, "E396", {"start": v(19.77, -18.15) * mm, "end": v(19.72, -18.13) * mm});
            skLineSegment(sketch, "E397", {"start": v(19.72, -18.13) * mm, "end": v(19.66, -18.11) * mm});
            skLineSegment(sketch, "E398", {"start": v(19.66, -18.11) * mm, "end": v(19.61, -18.1) * mm});
            skLineSegment(sketch, "E399", {"start": v(19.61, -18.1) * mm, "end": v(19.56, -18.08) * mm});
            skLineSegment(sketch, "E400", {"start": v(19.56, -18.08) * mm, "end": v(19.5, -18.07) * mm});
            skLineSegment(sketch, "E401", {"start": v(19.5, -18.07) * mm, "end": v(19.45, -18.06) * mm});
            skLineSegment(sketch, "E402", {"start": v(19.45, -18.06) * mm, "end": v(19.4, -18.05) * mm});
            skLineSegment(sketch, "E403", {"start": v(19.4, -18.05) * mm, "end": v(19.34, -18.04) * mm});
            skLineSegment(sketch, "E404", {"start": v(19.34, -18.04) * mm, "end": v(19.28, -18.04) * mm});
            skLineSegment(sketch, "E405", {"start": v(19.28, -18.04) * mm, "end": v(19.23, -18.03) * mm});
            skLineSegment(sketch, "E406", {"start": v(19.23, -18.03) * mm, "end": v(19.17, -18.03) * mm});
            skLineSegment(sketch, "E407", {"start": v(19.17, -18.03) * mm, "end": v(19.12, -18.03) * mm});
            skLineSegment(sketch, "E408", {"start": v(19.12, -18.03) * mm, "end": v(19.06, -18.03) * mm});
            skLineSegment(sketch, "E409", {"start": v(19.06, -18.03) * mm, "end": v(19, -18.04) * mm});
            skLineSegment(sketch, "E410", {"start": v(19, -18.04) * mm, "end": v(18.95, -18.04) * mm});
            skLineSegment(sketch, "E411", {"start": v(18.95, -18.04) * mm, "end": v(18.9, -18.05) * mm});
            skLineSegment(sketch, "E412", {"start": v(18.9, -18.05) * mm, "end": v(18.84, -18.06) * mm});
            skLineSegment(sketch, "E413", {"start": v(18.84, -18.06) * mm, "end": v(18.78, -18.07) * mm});
            skLineSegment(sketch, "E414", {"start": v(18.78, -18.07) * mm, "end": v(18.73, -18.09) * mm});
            skLineSegment(sketch, "E415", {"start": v(18.73, -18.09) * mm, "end": v(18.68, -18.1) * mm});
            skLineSegment(sketch, "E416", {"start": v(18.68, -18.1) * mm, "end": v(18.62, -18.12) * mm});
            skLineSegment(sketch, "E417", {"start": v(18.62, -18.12) * mm, "end": v(18.57, -18.14) * mm});
            skLineSegment(sketch, "E418", {"start": v(18.57, -18.14) * mm, "end": v(18.52, -18.16) * mm});
            skLineSegment(sketch, "E419", {"start": v(18.52, -18.16) * mm, "end": v(18.47, -18.18) * mm});
            skLineSegment(sketch, "E420", {"start": v(18.47, -18.18) * mm, "end": v(18.42, -18.2) * mm});
            skLineSegment(sketch, "E421", {"start": v(18.42, -18.2) * mm, "end": v(18.37, -18.23) * mm});
            skLineSegment(sketch, "E422", {"start": v(18.37, -18.23) * mm, "end": v(18.32, -18.26) * mm});
            skLineSegment(sketch, "E423", {"start": v(18.32, -18.26) * mm, "end": v(18.27, -18.3) * mm});
            skLineSegment(sketch, "E424", {"start": v(18.27, -18.3) * mm, "end": v(18.23, -18.32) * mm});
            skLineSegment(sketch, "E425", {"start": v(18.23, -18.32) * mm, "end": v(18.18, -18.36) * mm});
            skLineSegment(sketch, "E426", {"start": v(18.18, -18.36) * mm, "end": v(18.14, -18.4) * mm});
            skLineSegment(sketch, "E427", {"start": v(18.14, -18.4) * mm, "end": v(18.1, -18.43) * mm});
            skLineSegment(sketch, "E428", {"start": v(18.1, -18.43) * mm, "end": v(18.06, -18.46) * mm});
            skLineSegment(sketch, "E429", {"start": v(18.06, -18.46) * mm, "end": v(18.02, -18.5) * mm});
            skLineSegment(sketch, "E430", {"start": v(18.02, -18.5) * mm, "end": v(17.98, -18.54) * mm});
            skLineSegment(sketch, "E431", {"start": v(17.98, -18.54) * mm, "end": v(17.94, -18.58) * mm});
            skLineSegment(sketch, "E432", {"start": v(17.94, -18.58) * mm, "end": v(17.9, -18.63) * mm});
            skLineSegment(sketch, "E433", {"start": v(17.9, -18.63) * mm, "end": v(17.87, -18.67) * mm});
            skLineSegment(sketch, "E434", {"start": v(17.87, -18.67) * mm, "end": v(17.84, -18.72) * mm});
            skLineSegment(sketch, "E435", {"start": v(17.84, -18.72) * mm, "end": v(17.8, -18.76) * mm});
            skLineSegment(sketch, "E436", {"start": v(17.8, -18.76) * mm, "end": v(17.78, -18.8) * mm});
            skLineSegment(sketch, "E437", {"start": v(17.78, -18.8) * mm, "end": v(17.75, -18.86) * mm});
            skLineSegment(sketch, "E438", {"start": v(17.75, -18.86) * mm, "end": v(17.72, -18.9) * mm});
            skLineSegment(sketch, "E439", {"start": v(17.72, -18.9) * mm, "end": v(17.7, -18.96) * mm});
            skLineSegment(sketch, "E440", {"start": v(17.7, -18.96) * mm, "end": v(17.67, -19) * mm});
            skLineSegment(sketch, "E441", {"start": v(17.67, -19) * mm, "end": v(17.65, -19.06) * mm});
            skLineSegment(sketch, "E442", {"start": v(17.65, -19.06) * mm, "end": v(17.63, -19.11) * mm});
            skLineSegment(sketch, "E443", {"start": v(17.63, -19.11) * mm, "end": v(17.62, -19.16) * mm});
            skLineSegment(sketch, "E444", {"start": v(17.62, -19.16) * mm, "end": v(17.6, -19.22) * mm});
            skLineSegment(sketch, "E445", {"start": v(17.6, -19.22) * mm, "end": v(17.59, -19.27) * mm});
            skLineSegment(sketch, "E446", {"start": v(17.59, -19.27) * mm, "end": v(17.58, -19.33) * mm});
            skLineSegment(sketch, "E447", {"start": v(17.58, -19.33) * mm, "end": v(17.57, -19.38) * mm});
            skLineSegment(sketch, "E448", {"start": v(17.57, -19.38) * mm, "end": v(17.56, -19.44) * mm});
            skLineSegment(sketch, "E449", {"start": v(17.56, -19.44) * mm, "end": v(17.55, -19.5) * mm});
            skLineSegment(sketch, "E450", {"start": v(17.55, -19.5) * mm, "end": v(17.55, -19.55) * mm});
            skLineSegment(sketch, "E451", {"start": v(17.55, -19.55) * mm, "end": v(17.55, -19.6) * mm});
            skLineSegment(sketch, "E452", {"start": v(17.55, -19.6) * mm, "end": v(17.54, -19.66) * mm});
            skLineSegment(sketch, "E453", {"start": v(17.54, -19.66) * mm, "end": v(17.55, -19.71) * mm});
            skLineSegment(sketch, "E454", {"start": v(17.55, -19.71) * mm, "end": v(17.55, -19.77) * mm});
            skLineSegment(sketch, "E455", {"start": v(17.55, -19.77) * mm, "end": v(17.56, -19.82) * mm});
            skLineSegment(sketch, "E456", {"start": v(17.56, -19.82) * mm, "end": v(17.56, -19.88) * mm});
            skLineSegment(sketch, "E457", {"start": v(17.56, -19.88) * mm, "end": v(17.57, -19.93) * mm});
            skLineSegment(sketch, "E458", {"start": v(17.57, -19.93) * mm, "end": v(17.58, -19.99) * mm});
            skLineSegment(sketch, "E459", {"start": v(17.58, -19.99) * mm, "end": v(17.6, -20.04) * mm});
            skLineSegment(sketch, "E460", {"start": v(17.6, -20.04) * mm, "end": v(17.61, -20.1) * mm});
            skLineSegment(sketch, "E461", {"start": v(17.61, -20.1) * mm, "end": v(17.63, -20.15) * mm});
            skLineSegment(sketch, "E462", {"start": v(17.63, -20.15) * mm, "end": v(17.65, -20.2) * mm});
            skLineSegment(sketch, "E463", {"start": v(17.65, -20.2) * mm, "end": v(17.67, -20.25) * mm});
            skLineSegment(sketch, "E464", {"start": v(17.67, -20.25) * mm, "end": v(17.69, -20.3) * mm});
            skLineSegment(sketch, "E465", {"start": v(17.69, -20.3) * mm, "end": v(17.71, -20.36) * mm});
            skLineSegment(sketch, "E466", {"start": v(17.71, -20.36) * mm, "end": v(17.74, -20.4) * mm});
            skLineSegment(sketch, "E467", {"start": v(17.74, -20.4) * mm, "end": v(17.77, -20.45) * mm});
            skLineSegment(sketch, "E468", {"start": v(17.77, -20.45) * mm, "end": v(17.8, -20.5) * mm});
            skLineSegment(sketch, "E469", {"start": v(17.8, -20.5) * mm, "end": v(17.83, -20.55) * mm});
            skLineSegment(sketch, "E470", {"start": v(17.83, -20.55) * mm, "end": v(17.86, -20.6) * mm});
            skLineSegment(sketch, "E471", {"start": v(17.86, -20.6) * mm, "end": v(17.9, -20.64) * mm});
            skLineSegment(sketch, "E472", {"start": v(17.9, -20.64) * mm, "end": v(17.93, -20.68) * mm});
            skLineSegment(sketch, "E473", {"start": v(17.93, -20.68) * mm, "end": v(17.96, -20.72) * mm});
            skLineSegment(sketch, "E474", {"start": v(17.96, -20.72) * mm, "end": v(18, -20.76) * mm});
            skLineSegment(sketch, "E475", {"start": v(18, -20.76) * mm, "end": v(18.04, -20.8) * mm});
            skLineSegment(sketch, "E476", {"start": v(18.04, -20.8) * mm, "end": v(18.08, -20.84) * mm});
            skLineSegment(sketch, "E477", {"start": v(18.08, -20.84) * mm, "end": v(18.13, -20.88) * mm});
            skLineSegment(sketch, "E478", {"start": v(18.13, -20.88) * mm, "end": v(18.17, -20.91) * mm});
            skLineSegment(sketch, "E479", {"start": v(18.17, -20.91) * mm, "end": v(18.21, -20.94) * mm});
            skLineSegment(sketch, "E480", {"start": v(18.21, -20.94) * mm, "end": v(18.26, -20.98) * mm});
            skLineSegment(sketch, "E481", {"start": v(18.26, -20.98) * mm, "end": v(18.3, -21) * mm});
            skLineSegment(sketch, "E482", {"start": v(18.3, -21) * mm, "end": v(18.35, -21.03) * mm});
            skLineSegment(sketch, "E483", {"start": v(18.35, -21.03) * mm, "end": v(18.4, -21.06) * mm});
            skLineSegment(sketch, "E484", {"start": v(18.4, -21.06) * mm, "end": v(18.45, -21.09) * mm});
            skLineSegment(sketch, "E485", {"start": v(18.45, -21.09) * mm, "end": v(18.5, -21.11) * mm});
            skLineSegment(sketch, "E486", {"start": v(18.5, -21.11) * mm, "end": v(18.55, -21.13) * mm});
            skLineSegment(sketch, "E487", {"start": v(18.55, -21.13) * mm, "end": v(18.6, -21.15) * mm});
            skLineSegment(sketch, "E488", {"start": v(18.6, -21.15) * mm, "end": v(18.66, -21.17) * mm});
            skLineSegment(sketch, "E489", {"start": v(18.66, -21.17) * mm, "end": v(18.71, -21.19) * mm});
            skLineSegment(sketch, "E490", {"start": v(18.71, -21.19) * mm, "end": v(18.77, -21.2) * mm});
            skLineSegment(sketch, "E491", {"start": v(18.77, -21.2) * mm, "end": v(18.82, -21.21) * mm});
            skLineSegment(sketch, "E492", {"start": v(18.82, -21.21) * mm, "end": v(18.88, -21.22) * mm});
            skLineSegment(sketch, "E493", {"start": v(18.88, -21.22) * mm, "end": v(18.93, -21.23) * mm});
            skLineSegment(sketch, "E494", {"start": v(18.93, -21.23) * mm, "end": v(18.99, -21.24) * mm});
            skLineSegment(sketch, "E495", {"start": v(18.99, -21.24) * mm, "end": v(19.04, -21.24) * mm});
            skLineSegment(sketch, "E496", {"start": v(19.04, -21.24) * mm, "end": v(19.1, -21.25) * mm});
            skLineSegment(sketch, "E497", {"start": v(19.1, -21.25) * mm, "end": v(19.15, -21.25) * mm});
            skLineSegment(sketch, "E498", {"start": v(19.15, -21.25) * mm, "end": v(19.2, -21.25) * mm});
            skLineSegment(sketch, "E499", {"start": v(19.2, -21.25) * mm, "end": v(19.27, -21.24) * mm});
            skLineSegment(sketch, "E500", {"start": v(19.27, -21.24) * mm, "end": v(19.32, -21.24) * mm});
            skLineSegment(sketch, "E501", {"start": v(19.32, -21.24) * mm, "end": v(19.38, -21.23) * mm});
            skLineSegment(sketch, "E502", {"start": v(19.38, -21.23) * mm, "end": v(19.43, -21.22) * mm});
            skLineSegment(sketch, "E503", {"start": v(19.43, -21.22) * mm, "end": v(19.49, -21.21) * mm});
            skLineSegment(sketch, "E504", {"start": v(19.49, -21.21) * mm, "end": v(19.54, -21.2) * mm});
            skLineSegment(sketch, "E505", {"start": v(19.54, -21.2) * mm, "end": v(19.6, -21.18) * mm});
            skLineSegment(sketch, "E506", {"start": v(19.6, -21.18) * mm, "end": v(19.65, -21.17) * mm});
            skLineSegment(sketch, "E507", {"start": v(19.65, -21.17) * mm, "end": v(19.7, -21.15) * mm});
            skLineSegment(sketch, "E508", {"start": v(19.7, -21.15) * mm, "end": v(19.76, -21.13) * mm});
            skLineSegment(sketch, "E509", {"start": v(19.76, -21.13) * mm, "end": v(19.8, -21.1) * mm});
            skLineSegment(sketch, "E510", {"start": v(19.8, -21.1) * mm, "end": v(19.86, -21.08) * mm});
            skLineSegment(sketch, "E511", {"start": v(19.86, -21.08) * mm, "end": v(19.9, -21.06) * mm});
            skLineSegment(sketch, "E512", {"start": v(19.9, -21.06) * mm, "end": v(19.96, -21.03) * mm});
            skLineSegment(sketch, "E513", {"start": v(19.96, -21.03) * mm, "end": v(20, -21) * mm});
            skLineSegment(sketch, "E514", {"start": v(20, -21) * mm, "end": v(20.05, -20.97) * mm});
            skLineSegment(sketch, "E515", {"start": v(20.05, -20.97) * mm, "end": v(20.1, -20.94) * mm});
            skLineSegment(sketch, "E516", {"start": v(20.1, -20.94) * mm, "end": v(20.14, -20.9) * mm});
            skLineSegment(sketch, "E517", {"start": v(20.14, -20.9) * mm, "end": v(20.19, -20.87) * mm});
            skLineSegment(sketch, "E518", {"start": v(20.19, -20.87) * mm, "end": v(20.23, -20.83) * mm});
            skLineSegment(sketch, "E519", {"start": v(20.23, -20.83) * mm, "end": v(20.27, -20.8) * mm});
            skLineSegment(sketch, "E520", {"start": v(20.27, -20.8) * mm, "end": v(20.3, -20.76) * mm});
            skLineSegment(sketch, "E521", {"start": v(20.3, -20.76) * mm, "end": v(20.35, -20.72) * mm});
            skLineSegment(sketch, "E522", {"start": v(20.35, -20.72) * mm, "end": v(20.38, -20.67) * mm});
            skLineSegment(sketch, "E523", {"start": v(20.38, -20.67) * mm, "end": v(20.42, -20.63) * mm});
            skLineSegment(sketch, "E524", {"start": v(20.42, -20.63) * mm, "end": v(20.45, -20.58) * mm});
            skLineSegment(sketch, "E525", {"start": v(20.45, -20.58) * mm, "end": v(20.49, -20.54) * mm});
            skLineSegment(sketch, "E526", {"start": v(20.49, -20.54) * mm, "end": v(20.52, -20.5) * mm});
            skLineSegment(sketch, "E527", {"start": v(20.52, -20.5) * mm, "end": v(20.55, -20.44) * mm});
            skLineSegment(sketch, "E528", {"start": v(20.55, -20.44) * mm, "end": v(20.57, -20.4) * mm});
            skLineSegment(sketch, "E529", {"start": v(20.57, -20.4) * mm, "end": v(20.6, -20.34) * mm});
            skLineSegment(sketch, "E530", {"start": v(20.6, -20.34) * mm, "end": v(20.62, -20.3) * mm});
            skLineSegment(sketch, "E531", {"start": v(20.62, -20.3) * mm, "end": v(20.64, -20.24) * mm});
            skLineSegment(sketch, "E532", {"start": v(20.64, -20.24) * mm, "end": v(20.66, -20.19) * mm});
            skLineSegment(sketch, "E533", {"start": v(20.66, -20.19) * mm, "end": v(20.68, -20.14) * mm});
            skLineSegment(sketch, "E534", {"start": v(20.68, -20.14) * mm, "end": v(20.7, -20.08) * mm});
            skLineSegment(sketch, "E535", {"start": v(20.7, -20.08) * mm, "end": v(20.71, -20.03) * mm});
            skLineSegment(sketch, "E536", {"start": v(20.71, -20.03) * mm, "end": v(20.73, -19.97) * mm});
            skLineSegment(sketch, "E537", {"start": v(20.73, -19.97) * mm, "end": v(20.74, -19.92) * mm});
            skLineSegment(sketch, "E538", {"start": v(20.74, -19.92) * mm, "end": v(20.75, -19.86) * mm});
            skLineSegment(sketch, "E539", {"start": v(20.75, -19.86) * mm, "end": v(20.75, -19.8) * mm});
            skLineSegment(sketch, "E540", {"start": v(20.75, -19.8) * mm, "end": v(20.76, -19.75) * mm});
            skLineSegment(sketch, "E541", {"start": v(20.76, -19.75) * mm, "end": v(20.76, -19.7) * mm});
            skLineSegment(sketch, "E542", {"start": v(20.76, -19.7) * mm, "end": v(20.76, -19.64) * mm});
            skLineSegment(sketch, "E543", {"start": v(-61.72, -19.64) * mm, "end": v(-61.72, -19.58) * mm});
            skLineSegment(sketch, "E544", {"start": v(-61.72, -19.58) * mm, "end": v(-61.72, -19.53) * mm});
            skLineSegment(sketch, "E545", {"start": v(-61.72, -19.53) * mm, "end": v(-61.73, -19.47) * mm});
            skLineSegment(sketch, "E546", {"start": v(-61.73, -19.47) * mm, "end": v(-61.73, -19.42) * mm});
            skLineSegment(sketch, "E547", {"start": v(-61.73, -19.42) * mm, "end": v(-61.74, -19.36) * mm});
            skLineSegment(sketch, "E548", {"start": v(-61.74, -19.36) * mm, "end": v(-61.75, -19.3) * mm});
            skLineSegment(sketch, "E549", {"start": v(-61.75, -19.3) * mm, "end": v(-61.76, -19.25) * mm});
            skLineSegment(sketch, "E550", {"start": v(-61.76, -19.25) * mm, "end": v(-61.78, -19.2) * mm});
            skLineSegment(sketch, "E551", {"start": v(-61.78, -19.2) * mm, "end": v(-61.8, -19.15) * mm});
            skLineSegment(sketch, "E552", {"start": v(-61.8, -19.15) * mm, "end": v(-61.81, -19.1) * mm});
            skLineSegment(sketch, "E553", {"start": v(-61.81, -19.1) * mm, "end": v(-61.83, -19.04) * mm});
            skLineSegment(sketch, "E554", {"start": v(-61.83, -19.04) * mm, "end": v(-61.85, -18.99) * mm});
            skLineSegment(sketch, "E555", {"start": v(-61.85, -18.99) * mm, "end": v(-61.88, -18.94) * mm});
            skLineSegment(sketch, "E556", {"start": v(-61.88, -18.94) * mm, "end": v(-61.9, -18.89) * mm});
            skLineSegment(sketch, "E557", {"start": v(-61.9, -18.89) * mm, "end": v(-61.93, -18.84) * mm});
            skLineSegment(sketch, "E558", {"start": v(-61.93, -18.84) * mm, "end": v(-61.96, -18.8) * mm});
            skLineSegment(sketch, "E559", {"start": v(-61.96, -18.8) * mm, "end": v(-61.99, -18.75) * mm});
            skLineSegment(sketch, "E560", {"start": v(-61.99, -18.75) * mm, "end": v(-62.02, -18.7) * mm});
            skLineSegment(sketch, "E561", {"start": v(-62.02, -18.7) * mm, "end": v(-62.05, -18.66) * mm});
            skLineSegment(sketch, "E562", {"start": v(-62.05, -18.66) * mm, "end": v(-62.09, -18.61) * mm});
            skLineSegment(sketch, "E563", {"start": v(-62.09, -18.61) * mm, "end": v(-62.12, -18.57) * mm});
            skLineSegment(sketch, "E564", {"start": v(-62.12, -18.57) * mm, "end": v(-62.16, -18.53) * mm});
            skLineSegment(sketch, "E565", {"start": v(-62.16, -18.53) * mm, "end": v(-62.2, -18.49) * mm});
            skLineSegment(sketch, "E566", {"start": v(-62.2, -18.49) * mm, "end": v(-62.24, -18.45) * mm});
            skLineSegment(sketch, "E567", {"start": v(-62.24, -18.45) * mm, "end": v(-62.28, -18.41) * mm});
            skLineSegment(sketch, "E568", {"start": v(-62.28, -18.41) * mm, "end": v(-62.33, -18.38) * mm});
            skLineSegment(sketch, "E569", {"start": v(-62.33, -18.38) * mm, "end": v(-62.37, -18.34) * mm});
            skLineSegment(sketch, "E570", {"start": v(-62.37, -18.34) * mm, "end": v(-62.42, -18.31) * mm});
            skLineSegment(sketch, "E571", {"start": v(-62.42, -18.31) * mm, "end": v(-62.46, -18.28) * mm});
            skLineSegment(sketch, "E572", {"start": v(-62.46, -18.28) * mm, "end": v(-62.51, -18.25) * mm});
            skLineSegment(sketch, "E573", {"start": v(-62.51, -18.25) * mm, "end": v(-62.56, -18.23) * mm});
            skLineSegment(sketch, "E574", {"start": v(-62.56, -18.23) * mm, "end": v(-62.6, -18.2) * mm});
            skLineSegment(sketch, "E575", {"start": v(-62.6, -18.2) * mm, "end": v(-62.66, -18.18) * mm});
            skLineSegment(sketch, "E576", {"start": v(-62.66, -18.18) * mm, "end": v(-62.71, -18.15) * mm});
            skLineSegment(sketch, "E577", {"start": v(-62.71, -18.15) * mm, "end": v(-62.76, -18.13) * mm});
            skLineSegment(sketch, "E578", {"start": v(-62.76, -18.13) * mm, "end": v(-62.81, -18.11) * mm});
            skLineSegment(sketch, "E579", {"start": v(-62.81, -18.11) * mm, "end": v(-62.87, -18.1) * mm});
            skLineSegment(sketch, "E580", {"start": v(-62.87, -18.1) * mm, "end": v(-62.92, -18.08) * mm});
            skLineSegment(sketch, "E581", {"start": v(-62.92, -18.08) * mm, "end": v(-62.98, -18.07) * mm});
            skLineSegment(sketch, "E582", {"start": v(-62.98, -18.07) * mm, "end": v(-63.03, -18.06) * mm});
            skLineSegment(sketch, "E583", {"start": v(-63.03, -18.06) * mm, "end": v(-63.09, -18.05) * mm});
            skLineSegment(sketch, "E584", {"start": v(-63.09, -18.05) * mm, "end": v(-63.14, -18.04) * mm});
            skLineSegment(sketch, "E585", {"start": v(-63.14, -18.04) * mm, "end": v(-63.2, -18.04) * mm});
            skLineSegment(sketch, "E586", {"start": v(-63.2, -18.04) * mm, "end": v(-63.25, -18.03) * mm});
            skLineSegment(sketch, "E587", {"start": v(-63.25, -18.03) * mm, "end": v(-63.3, -18.03) * mm});
            skLineSegment(sketch, "E588", {"start": v(-63.3, -18.03) * mm, "end": v(-63.36, -18.03) * mm});
            skLineSegment(sketch, "E589", {"start": v(-63.36, -18.03) * mm, "end": v(-63.42, -18.03) * mm});
            skLineSegment(sketch, "E590", {"start": v(-63.42, -18.03) * mm, "end": v(-63.47, -18.04) * mm});
            skLineSegment(sketch, "E591", {"start": v(-63.47, -18.04) * mm, "end": v(-63.53, -18.04) * mm});
            skLineSegment(sketch, "E592", {"start": v(-63.53, -18.04) * mm, "end": v(-63.58, -18.05) * mm});
            skLineSegment(sketch, "E593", {"start": v(-63.58, -18.05) * mm, "end": v(-63.64, -18.06) * mm});
            skLineSegment(sketch, "E594", {"start": v(-63.64, -18.06) * mm, "end": v(-63.7, -18.07) * mm});
            skLineSegment(sketch, "E595", {"start": v(-63.7, -18.07) * mm, "end": v(-63.75, -18.09) * mm});
            skLineSegment(sketch, "E596", {"start": v(-63.75, -18.09) * mm, "end": v(-63.8, -18.1) * mm});
            skLineSegment(sketch, "E597", {"start": v(-63.8, -18.1) * mm, "end": v(-63.85, -18.12) * mm});
            skLineSegment(sketch, "E598", {"start": v(-63.85, -18.12) * mm, "end": v(-63.9, -18.14) * mm});
            skLineSegment(sketch, "E599", {"start": v(-63.9, -18.14) * mm, "end": v(-63.96, -18.16) * mm});
            skLineSegment(sketch, "E600", {"start": v(-63.96, -18.16) * mm, "end": v(-64, -18.18) * mm});
            skLineSegment(sketch, "E601", {"start": v(-64, -18.18) * mm, "end": v(-64.06, -18.2) * mm});
            skLineSegment(sketch, "E602", {"start": v(-64.06, -18.2) * mm, "end": v(-64.1, -18.23) * mm});
            skLineSegment(sketch, "E603", {"start": v(-64.1, -18.23) * mm, "end": v(-64.16, -18.26) * mm});
            skLineSegment(sketch, "E604", {"start": v(-64.16, -18.26) * mm, "end": v(-64.2, -18.3) * mm});
            skLineSegment(sketch, "E605", {"start": v(-64.2, -18.3) * mm, "end": v(-64.25, -18.32) * mm});
            skLineSegment(sketch, "E606", {"start": v(-64.25, -18.32) * mm, "end": v(-64.3, -18.36) * mm});
            skLineSegment(sketch, "E607", {"start": v(-64.3, -18.36) * mm, "end": v(-64.34, -18.4) * mm});
            skLineSegment(sketch, "E608", {"start": v(-64.34, -18.4) * mm, "end": v(-64.38, -18.43) * mm});
            skLineSegment(sketch, "E609", {"start": v(-64.38, -18.43) * mm, "end": v(-64.42, -18.46) * mm});
            skLineSegment(sketch, "E610", {"start": v(-64.42, -18.46) * mm, "end": v(-64.46, -18.5) * mm});
            skLineSegment(sketch, "E611", {"start": v(-64.46, -18.5) * mm, "end": v(-64.5, -18.54) * mm});
            skLineSegment(sketch, "E612", {"start": v(-64.5, -18.54) * mm, "end": v(-64.54, -18.58) * mm});
            skLineSegment(sketch, "E613", {"start": v(-64.54, -18.58) * mm, "end": v(-64.57, -18.63) * mm});
            skLineSegment(sketch, "E614", {"start": v(-64.57, -18.63) * mm, "end": v(-64.6, -18.67) * mm});
            skLineSegment(sketch, "E615", {"start": v(-64.6, -18.67) * mm, "end": v(-64.64, -18.72) * mm});
            skLineSegment(sketch, "E616", {"start": v(-64.64, -18.72) * mm, "end": v(-64.67, -18.76) * mm});
            skLineSegment(sketch, "E617", {"start": v(-64.67, -18.76) * mm, "end": v(-64.7, -18.8) * mm});
            skLineSegment(sketch, "E618", {"start": v(-64.7, -18.8) * mm, "end": v(-64.73, -18.86) * mm});
            skLineSegment(sketch, "E619", {"start": v(-64.73, -18.86) * mm, "end": v(-64.76, -18.9) * mm});
            skLineSegment(sketch, "E620", {"start": v(-64.76, -18.9) * mm, "end": v(-64.78, -18.96) * mm});
            skLineSegment(sketch, "E621", {"start": v(-64.78, -18.96) * mm, "end": v(-64.8, -19) * mm});
            skLineSegment(sketch, "E622", {"start": v(-64.8, -19) * mm, "end": v(-64.83, -19.06) * mm});
            skLineSegment(sketch, "E623", {"start": v(-64.83, -19.06) * mm, "end": v(-64.84, -19.11) * mm});
            skLineSegment(sketch, "E624", {"start": v(-64.84, -19.11) * mm, "end": v(-64.86, -19.16) * mm});
            skLineSegment(sketch, "E625", {"start": v(-64.86, -19.16) * mm, "end": v(-64.88, -19.22) * mm});
            skLineSegment(sketch, "E626", {"start": v(-64.88, -19.22) * mm, "end": v(-64.9, -19.27) * mm});
            skLineSegment(sketch, "E627", {"start": v(-64.9, -19.27) * mm, "end": v(-64.9, -19.33) * mm});
            skLineSegment(sketch, "E628", {"start": v(-64.9, -19.33) * mm, "end": v(-64.91, -19.38) * mm});
            skLineSegment(sketch, "E629", {"start": v(-64.91, -19.38) * mm, "end": v(-64.92, -19.44) * mm});
            skLineSegment(sketch, "E630", {"start": v(-64.92, -19.44) * mm, "end": v(-64.93, -19.5) * mm});
            skLineSegment(sketch, "E631", {"start": v(-64.93, -19.5) * mm, "end": v(-64.93, -19.55) * mm});
            skLineSegment(sketch, "E632", {"start": v(-64.93, -19.55) * mm, "end": v(-64.93, -19.6) * mm});
            skLineSegment(sketch, "E633", {"start": v(-64.93, -19.6) * mm, "end": v(-64.93, -19.66) * mm});
            skLineSegment(sketch, "E634", {"start": v(-64.93, -19.66) * mm, "end": v(-64.93, -19.71) * mm});
            skLineSegment(sketch, "E635", {"start": v(-64.93, -19.71) * mm, "end": v(-64.93, -19.77) * mm});
            skLineSegment(sketch, "E636", {"start": v(-64.93, -19.77) * mm, "end": v(-64.92, -19.82) * mm});
            skLineSegment(sketch, "E637", {"start": v(-64.92, -19.82) * mm, "end": v(-64.92, -19.88) * mm});
            skLineSegment(sketch, "E638", {"start": v(-64.92, -19.88) * mm, "end": v(-64.9, -19.93) * mm});
            skLineSegment(sketch, "E639", {"start": v(-64.9, -19.93) * mm, "end": v(-64.9, -19.99) * mm});
            skLineSegment(sketch, "E640", {"start": v(-64.9, -19.99) * mm, "end": v(-64.88, -20.04) * mm});
            skLineSegment(sketch, "E641", {"start": v(-64.88, -20.04) * mm, "end": v(-64.87, -20.1) * mm});
            skLineSegment(sketch, "E642", {"start": v(-64.87, -20.1) * mm, "end": v(-64.85, -20.15) * mm});
            skLineSegment(sketch, "E643", {"start": v(-64.85, -20.15) * mm, "end": v(-64.83, -20.2) * mm});
            skLineSegment(sketch, "E644", {"start": v(-64.83, -20.2) * mm, "end": v(-64.81, -20.25) * mm});
            skLineSegment(sketch, "E645", {"start": v(-64.81, -20.25) * mm, "end": v(-64.79, -20.3) * mm});
            skLineSegment(sketch, "E646", {"start": v(-64.79, -20.3) * mm, "end": v(-64.77, -20.36) * mm});
            skLineSegment(sketch, "E647", {"start": v(-64.77, -20.36) * mm, "end": v(-64.74, -20.4) * mm});
            skLineSegment(sketch, "E648", {"start": v(-64.74, -20.4) * mm, "end": v(-64.71, -20.45) * mm});
            skLineSegment(sketch, "E649", {"start": v(-64.71, -20.45) * mm, "end": v(-64.68, -20.5) * mm});
            skLineSegment(sketch, "E650", {"start": v(-64.68, -20.5) * mm, "end": v(-64.65, -20.55) * mm});
            skLineSegment(sketch, "E651", {"start": v(-64.65, -20.55) * mm, "end": v(-64.62, -20.6) * mm});
            skLineSegment(sketch, "E652", {"start": v(-64.62, -20.6) * mm, "end": v(-64.59, -20.64) * mm});
            skLineSegment(sketch, "E653", {"start": v(-64.59, -20.64) * mm, "end": v(-64.55, -20.68) * mm});
            skLineSegment(sketch, "E654", {"start": v(-64.55, -20.68) * mm, "end": v(-64.51, -20.72) * mm});
            skLineSegment(sketch, "E655", {"start": v(-64.51, -20.72) * mm, "end": v(-64.48, -20.76) * mm});
            skLineSegment(sketch, "E656", {"start": v(-64.48, -20.76) * mm, "end": v(-64.44, -20.8) * mm});
            skLineSegment(sketch, "E657", {"start": v(-64.44, -20.8) * mm, "end": v(-64.4, -20.84) * mm});
            skLineSegment(sketch, "E658", {"start": v(-64.4, -20.84) * mm, "end": v(-64.35, -20.88) * mm});
            skLineSegment(sketch, "E659", {"start": v(-64.35, -20.88) * mm, "end": v(-64.3, -20.91) * mm});
            skLineSegment(sketch, "E660", {"start": v(-64.3, -20.91) * mm, "end": v(-64.26, -20.94) * mm});
            skLineSegment(sketch, "E661", {"start": v(-64.26, -20.94) * mm, "end": v(-64.22, -20.98) * mm});
            skLineSegment(sketch, "E662", {"start": v(-64.22, -20.98) * mm, "end": v(-64.17, -21) * mm});
            skLineSegment(sketch, "E663", {"start": v(-64.17, -21) * mm, "end": v(-64.12, -21.03) * mm});
            skLineSegment(sketch, "E664", {"start": v(-64.12, -21.03) * mm, "end": v(-64.08, -21.06) * mm});
            skLineSegment(sketch, "E665", {"start": v(-64.08, -21.06) * mm, "end": v(-64.03, -21.09) * mm});
            skLineSegment(sketch, "E666", {"start": v(-64.03, -21.09) * mm, "end": v(-63.98, -21.11) * mm});
            skLineSegment(sketch, "E667", {"start": v(-63.98, -21.11) * mm, "end": v(-63.92, -21.13) * mm});
            skLineSegment(sketch, "E668", {"start": v(-63.92, -21.13) * mm, "end": v(-63.87, -21.15) * mm});
            skLineSegment(sketch, "E669", {"start": v(-63.87, -21.15) * mm, "end": v(-63.82, -21.17) * mm});
            skLineSegment(sketch, "E670", {"start": v(-63.82, -21.17) * mm, "end": v(-63.77, -21.19) * mm});
            skLineSegment(sketch, "E671", {"start": v(-63.77, -21.19) * mm, "end": v(-63.71, -21.2) * mm});
            skLineSegment(sketch, "E672", {"start": v(-63.71, -21.2) * mm, "end": v(-63.66, -21.21) * mm});
            skLineSegment(sketch, "E673", {"start": v(-63.66, -21.21) * mm, "end": v(-63.6, -21.22) * mm});
            skLineSegment(sketch, "E674", {"start": v(-63.6, -21.22) * mm, "end": v(-63.55, -21.23) * mm});
            skLineSegment(sketch, "E675", {"start": v(-63.55, -21.23) * mm, "end": v(-63.5, -21.24) * mm});
            skLineSegment(sketch, "E676", {"start": v(-63.5, -21.24) * mm, "end": v(-63.44, -21.24) * mm});
            skLineSegment(sketch, "E677", {"start": v(-63.44, -21.24) * mm, "end": v(-63.38, -21.25) * mm});
            skLineSegment(sketch, "E678", {"start": v(-63.38, -21.25) * mm, "end": v(-63.33, -21.25) * mm});
            skLineSegment(sketch, "E679", {"start": v(-63.33, -21.25) * mm, "end": v(-63.27, -21.25) * mm});
            skLineSegment(sketch, "E680", {"start": v(-63.27, -21.25) * mm, "end": v(-63.21, -21.24) * mm});
            skLineSegment(sketch, "E681", {"start": v(-63.21, -21.24) * mm, "end": v(-63.16, -21.24) * mm});
            skLineSegment(sketch, "E682", {"start": v(-63.16, -21.24) * mm, "end": v(-63.1, -21.23) * mm});
            skLineSegment(sketch, "E683", {"start": v(-63.1, -21.23) * mm, "end": v(-63.05, -21.22) * mm});
            skLineSegment(sketch, "E684", {"start": v(-63.05, -21.22) * mm, "end": v(-63, -21.21) * mm});
            skLineSegment(sketch, "E685", {"start": v(-63, -21.21) * mm, "end": v(-62.94, -21.2) * mm});
            skLineSegment(sketch, "E686", {"start": v(-62.94, -21.2) * mm, "end": v(-62.88, -21.18) * mm});
            skLineSegment(sketch, "E687", {"start": v(-62.88, -21.18) * mm, "end": v(-62.83, -21.17) * mm});
            skLineSegment(sketch, "E688", {"start": v(-62.83, -21.17) * mm, "end": v(-62.78, -21.15) * mm});
            skLineSegment(sketch, "E689", {"start": v(-62.78, -21.15) * mm, "end": v(-62.72, -21.13) * mm});
            skLineSegment(sketch, "E690", {"start": v(-62.72, -21.13) * mm, "end": v(-62.67, -21.1) * mm});
            skLineSegment(sketch, "E691", {"start": v(-62.67, -21.1) * mm, "end": v(-62.62, -21.08) * mm});
            skLineSegment(sketch, "E692", {"start": v(-62.62, -21.08) * mm, "end": v(-62.57, -21.06) * mm});
            skLineSegment(sketch, "E693", {"start": v(-62.57, -21.06) * mm, "end": v(-62.52, -21.03) * mm});
            skLineSegment(sketch, "E694", {"start": v(-62.52, -21.03) * mm, "end": v(-62.47, -21) * mm});
            skLineSegment(sketch, "E695", {"start": v(-62.47, -21) * mm, "end": v(-62.43, -20.97) * mm});
            skLineSegment(sketch, "E696", {"start": v(-62.43, -20.97) * mm, "end": v(-62.38, -20.94) * mm});
            skLineSegment(sketch, "E697", {"start": v(-62.38, -20.94) * mm, "end": v(-62.34, -20.9) * mm});
            skLineSegment(sketch, "E698", {"start": v(-62.34, -20.9) * mm, "end": v(-62.3, -20.87) * mm});
            skLineSegment(sketch, "E699", {"start": v(-62.3, -20.87) * mm, "end": v(-62.25, -20.83) * mm});
            skLineSegment(sketch, "E700", {"start": v(-62.25, -20.83) * mm, "end": v(-62.2, -20.8) * mm});
            skLineSegment(sketch, "E701", {"start": v(-62.2, -20.8) * mm, "end": v(-62.17, -20.76) * mm});
            skLineSegment(sketch, "E702", {"start": v(-62.17, -20.76) * mm, "end": v(-62.13, -20.72) * mm});
            skLineSegment(sketch, "E703", {"start": v(-62.13, -20.72) * mm, "end": v(-62.1, -20.67) * mm});
            skLineSegment(sketch, "E704", {"start": v(-62.1, -20.67) * mm, "end": v(-62.06, -20.63) * mm});
            skLineSegment(sketch, "E705", {"start": v(-62.06, -20.63) * mm, "end": v(-62.02, -20.58) * mm});
            skLineSegment(sketch, "E706", {"start": v(-62.02, -20.58) * mm, "end": v(-62, -20.54) * mm});
            skLineSegment(sketch, "E707", {"start": v(-62, -20.54) * mm, "end": v(-61.96, -20.5) * mm});
            skLineSegment(sketch, "E708", {"start": v(-61.96, -20.5) * mm, "end": v(-61.93, -20.44) * mm});
            skLineSegment(sketch, "E709", {"start": v(-61.93, -20.44) * mm, "end": v(-61.9, -20.4) * mm});
            skLineSegment(sketch, "E710", {"start": v(-61.9, -20.4) * mm, "end": v(-61.88, -20.34) * mm});
            skLineSegment(sketch, "E711", {"start": v(-61.88, -20.34) * mm, "end": v(-61.86, -20.3) * mm});
            skLineSegment(sketch, "E712", {"start": v(-61.86, -20.3) * mm, "end": v(-61.83, -20.24) * mm});
            skLineSegment(sketch, "E713", {"start": v(-61.83, -20.24) * mm, "end": v(-61.81, -20.19) * mm});
            skLineSegment(sketch, "E714", {"start": v(-61.81, -20.19) * mm, "end": v(-61.8, -20.14) * mm});
            skLineSegment(sketch, "E715", {"start": v(-61.8, -20.14) * mm, "end": v(-61.78, -20.08) * mm});
            skLineSegment(sketch, "E716", {"start": v(-61.78, -20.08) * mm, "end": v(-61.77, -20.03) * mm});
            skLineSegment(sketch, "E717", {"start": v(-61.77, -20.03) * mm, "end": v(-61.75, -19.97) * mm});
            skLineSegment(sketch, "E718", {"start": v(-61.75, -19.97) * mm, "end": v(-61.74, -19.92) * mm});
            skLineSegment(sketch, "E719", {"start": v(-61.74, -19.92) * mm, "end": v(-61.73, -19.86) * mm});
            skLineSegment(sketch, "E720", {"start": v(-61.73, -19.86) * mm, "end": v(-61.73, -19.8) * mm});
            skLineSegment(sketch, "E721", {"start": v(-61.73, -19.8) * mm, "end": v(-61.72, -19.75) * mm});
            skLineSegment(sketch, "E722", {"start": v(-61.72, -19.75) * mm, "end": v(-61.72, -19.7) * mm});
            skLineSegment(sketch, "E723", {"start": v(-61.72, -19.7) * mm, "end": v(-61.72, -19.64) * mm});
            skLineSegment(sketch, "E724", {"start": v(-60.45, 28.58) * mm, "end": v(-60.45, 28.64) * mm});
            skLineSegment(sketch, "E725", {"start": v(-60.45, 28.64) * mm, "end": v(-60.45, 28.7) * mm});
            skLineSegment(sketch, "E726", {"start": v(-60.45, 28.7) * mm, "end": v(-60.46, 28.75) * mm});
            skLineSegment(sketch, "E727", {"start": v(-60.46, 28.75) * mm, "end": v(-60.46, 28.8) * mm});
            skLineSegment(sketch, "E728", {"start": v(-60.46, 28.8) * mm, "end": v(-60.47, 28.86) * mm});
            skLineSegment(sketch, "E729", {"start": v(-60.47, 28.86) * mm, "end": v(-60.48, 28.91) * mm});
            skLineSegment(sketch, "E730", {"start": v(-60.48, 28.91) * mm, "end": v(-60.5, 28.97) * mm});
            skLineSegment(sketch, "E731", {"start": v(-60.5, 28.97) * mm, "end": v(-60.5, 29.02) * mm});
            skLineSegment(sketch, "E732", {"start": v(-60.5, 29.02) * mm, "end": v(-60.53, 29.08) * mm});
            skLineSegment(sketch, "E733", {"start": v(-60.53, 29.08) * mm, "end": v(-60.54, 29.13) * mm});
            skLineSegment(sketch, "E734", {"start": v(-60.54, 29.13) * mm, "end": v(-60.56, 29.18) * mm});
            skLineSegment(sketch, "E735", {"start": v(-60.56, 29.18) * mm, "end": v(-60.59, 29.23) * mm});
            skLineSegment(sketch, "E736", {"start": v(-60.59, 29.23) * mm, "end": v(-60.6, 29.28) * mm});
            skLineSegment(sketch, "E737", {"start": v(-60.6, 29.28) * mm, "end": v(-60.63, 29.33) * mm});
            skLineSegment(sketch, "E738", {"start": v(-60.63, 29.33) * mm, "end": v(-60.66, 29.38) * mm});
            skLineSegment(sketch, "E739", {"start": v(-60.66, 29.38) * mm, "end": v(-60.69, 29.43) * mm});
            skLineSegment(sketch, "E740", {"start": v(-60.69, 29.43) * mm, "end": v(-60.72, 29.48) * mm});
            skLineSegment(sketch, "E741", {"start": v(-60.72, 29.48) * mm, "end": v(-60.75, 29.52) * mm});
            skLineSegment(sketch, "E742", {"start": v(-60.75, 29.52) * mm, "end": v(-60.78, 29.57) * mm});
            skLineSegment(sketch, "E743", {"start": v(-60.78, 29.57) * mm, "end": v(-60.82, 29.6) * mm});
            skLineSegment(sketch, "E744", {"start": v(-60.82, 29.6) * mm, "end": v(-60.86, 29.65) * mm});
            skLineSegment(sketch, "E745", {"start": v(-60.86, 29.65) * mm, "end": v(-60.9, 29.7) * mm});
            skLineSegment(sketch, "E746", {"start": v(-60.9, 29.7) * mm, "end": v(-60.93, 29.73) * mm});
            skLineSegment(sketch, "E747", {"start": v(-60.93, 29.73) * mm, "end": v(-60.97, 29.77) * mm});
            skLineSegment(sketch, "E748", {"start": v(-60.97, 29.77) * mm, "end": v(-61.01, 29.8) * mm});
            skLineSegment(sketch, "E749", {"start": v(-61.01, 29.8) * mm, "end": v(-61.06, 29.84) * mm});
            skLineSegment(sketch, "E750", {"start": v(-61.06, 29.84) * mm, "end": v(-61.1, 29.88) * mm});
            skLineSegment(sketch, "E751", {"start": v(-61.1, 29.88) * mm, "end": v(-61.15, 29.9) * mm});
            skLineSegment(sketch, "E752", {"start": v(-61.15, 29.9) * mm, "end": v(-61.2, 29.94) * mm});
            skLineSegment(sketch, "E753", {"start": v(-61.2, 29.94) * mm, "end": v(-61.24, 29.97) * mm});
            skLineSegment(sketch, "E754", {"start": v(-61.24, 29.97) * mm, "end": v(-61.29, 30) * mm});
            skLineSegment(sketch, "E755", {"start": v(-61.29, 30) * mm, "end": v(-61.34, 30.02) * mm});
            skLineSegment(sketch, "E756", {"start": v(-61.34, 30.02) * mm, "end": v(-61.39, 30.05) * mm});
            skLineSegment(sketch, "E757", {"start": v(-61.39, 30.05) * mm, "end": v(-61.44, 30.07) * mm});
            skLineSegment(sketch, "E758", {"start": v(-61.44, 30.07) * mm, "end": v(-61.5, 30.09) * mm});
            skLineSegment(sketch, "E759", {"start": v(-61.5, 30.09) * mm, "end": v(-61.55, 30.1) * mm});
            skLineSegment(sketch, "E760", {"start": v(-61.55, 30.1) * mm, "end": v(-61.6, 30.12) * mm});
            skLineSegment(sketch, "E761", {"start": v(-61.6, 30.12) * mm, "end": v(-61.65, 30.14) * mm});
            skLineSegment(sketch, "E762", {"start": v(-61.65, 30.14) * mm, "end": v(-61.7, 30.15) * mm});
            skLineSegment(sketch, "E763", {"start": v(-61.7, 30.15) * mm, "end": v(-61.76, 30.16) * mm});
            skLineSegment(sketch, "E764", {"start": v(-61.76, 30.16) * mm, "end": v(-61.82, 30.17) * mm});
            skLineSegment(sketch, "E765", {"start": v(-61.82, 30.17) * mm, "end": v(-61.87, 30.18) * mm});
            skLineSegment(sketch, "E766", {"start": v(-61.87, 30.18) * mm, "end": v(-61.93, 30.19) * mm});
            skLineSegment(sketch, "E767", {"start": v(-61.93, 30.19) * mm, "end": v(-61.98, 30.19) * mm});
            skLineSegment(sketch, "E768", {"start": v(-61.98, 30.19) * mm, "end": v(-62.04, 30.2) * mm});
            skLineSegment(sketch, "E769", {"start": v(-62.04, 30.2) * mm, "end": v(-62.1, 30.2) * mm});
            skLineSegment(sketch, "E770", {"start": v(-62.1, 30.2) * mm, "end": v(-62.15, 30.19) * mm});
            skLineSegment(sketch, "E771", {"start": v(-62.15, 30.19) * mm, "end": v(-62.2, 30.18) * mm});
            skLineSegment(sketch, "E772", {"start": v(-62.2, 30.18) * mm, "end": v(-62.26, 30.18) * mm});
            skLineSegment(sketch, "E773", {"start": v(-62.26, 30.18) * mm, "end": v(-62.31, 30.17) * mm});
            skLineSegment(sketch, "E774", {"start": v(-62.31, 30.17) * mm, "end": v(-62.37, 30.16) * mm});
            skLineSegment(sketch, "E775", {"start": v(-62.37, 30.16) * mm, "end": v(-62.42, 30.15) * mm});
            skLineSegment(sketch, "E776", {"start": v(-62.42, 30.15) * mm, "end": v(-62.48, 30.13) * mm});
            skLineSegment(sketch, "E777", {"start": v(-62.48, 30.13) * mm, "end": v(-62.53, 30.12) * mm});
            skLineSegment(sketch, "E778", {"start": v(-62.53, 30.12) * mm, "end": v(-62.58, 30.1) * mm});
            skLineSegment(sketch, "E779", {"start": v(-62.58, 30.1) * mm, "end": v(-62.64, 30.08) * mm});
            skLineSegment(sketch, "E780", {"start": v(-62.64, 30.08) * mm, "end": v(-62.69, 30.06) * mm});
            skLineSegment(sketch, "E781", {"start": v(-62.69, 30.06) * mm, "end": v(-62.74, 30.04) * mm});
            skLineSegment(sketch, "E782", {"start": v(-62.74, 30.04) * mm, "end": v(-62.79, 30.01) * mm});
            skLineSegment(sketch, "E783", {"start": v(-62.79, 30.01) * mm, "end": v(-62.84, 29.99) * mm});
            skLineSegment(sketch, "E784", {"start": v(-62.84, 29.99) * mm, "end": v(-62.89, 29.96) * mm});
            skLineSegment(sketch, "E785", {"start": v(-62.89, 29.96) * mm, "end": v(-62.93, 29.93) * mm});
            skLineSegment(sketch, "E786", {"start": v(-62.93, 29.93) * mm, "end": v(-62.98, 29.9) * mm});
            skLineSegment(sketch, "E787", {"start": v(-62.98, 29.9) * mm, "end": v(-63.03, 29.87) * mm});
            skLineSegment(sketch, "E788", {"start": v(-63.03, 29.87) * mm, "end": v(-63.07, 29.83) * mm});
            skLineSegment(sketch, "E789", {"start": v(-63.07, 29.83) * mm, "end": v(-63.11, 29.8) * mm});
            skLineSegment(sketch, "E790", {"start": v(-63.11, 29.8) * mm, "end": v(-63.15, 29.76) * mm});
            skLineSegment(sketch, "E791", {"start": v(-63.15, 29.76) * mm, "end": v(-63.2, 29.72) * mm});
            skLineSegment(sketch, "E792", {"start": v(-63.2, 29.72) * mm, "end": v(-63.23, 29.68) * mm});
            skLineSegment(sketch, "E793", {"start": v(-63.23, 29.68) * mm, "end": v(-63.27, 29.64) * mm});
            skLineSegment(sketch, "E794", {"start": v(-63.27, 29.64) * mm, "end": v(-63.3, 29.6) * mm});
            skLineSegment(sketch, "E795", {"start": v(-63.3, 29.6) * mm, "end": v(-63.34, 29.55) * mm});
            skLineSegment(sketch, "E796", {"start": v(-63.34, 29.55) * mm, "end": v(-63.37, 29.5) * mm});
            skLineSegment(sketch, "E797", {"start": v(-63.37, 29.5) * mm, "end": v(-63.4, 29.46) * mm});
            skLineSegment(sketch, "E798", {"start": v(-63.4, 29.46) * mm, "end": v(-63.43, 29.41) * mm});
            skLineSegment(sketch, "E799", {"start": v(-63.43, 29.41) * mm, "end": v(-63.46, 29.37) * mm});
            skLineSegment(sketch, "E800", {"start": v(-63.46, 29.37) * mm, "end": v(-63.49, 29.32) * mm});
            skLineSegment(sketch, "E801", {"start": v(-63.49, 29.32) * mm, "end": v(-63.51, 29.27) * mm});
            skLineSegment(sketch, "E802", {"start": v(-63.51, 29.27) * mm, "end": v(-63.53, 29.22) * mm});
            skLineSegment(sketch, "E803", {"start": v(-63.53, 29.22) * mm, "end": v(-63.56, 29.16) * mm});
            skLineSegment(sketch, "E804", {"start": v(-63.56, 29.16) * mm, "end": v(-63.57, 29.11) * mm});
            skLineSegment(sketch, "E805", {"start": v(-63.57, 29.11) * mm, "end": v(-63.6, 29.06) * mm});
            skLineSegment(sketch, "E806", {"start": v(-63.6, 29.06) * mm, "end": v(-63.6, 29) * mm});
            skLineSegment(sketch, "E807", {"start": v(-63.6, 29) * mm, "end": v(-63.62, 28.95) * mm});
            skLineSegment(sketch, "E808", {"start": v(-63.62, 28.95) * mm, "end": v(-63.63, 28.9) * mm});
            skLineSegment(sketch, "E809", {"start": v(-63.63, 28.9) * mm, "end": v(-63.64, 28.84) * mm});
            skLineSegment(sketch, "E810", {"start": v(-63.64, 28.84) * mm, "end": v(-63.65, 28.79) * mm});
            skLineSegment(sketch, "E811", {"start": v(-63.65, 28.79) * mm, "end": v(-63.66, 28.73) * mm});
            skLineSegment(sketch, "E812", {"start": v(-63.66, 28.73) * mm, "end": v(-63.66, 28.68) * mm});
            skLineSegment(sketch, "E813", {"start": v(-63.66, 28.68) * mm, "end": v(-63.66, 28.62) * mm});
            skLineSegment(sketch, "E814", {"start": v(-63.66, 28.62) * mm, "end": v(-63.66, 28.56) * mm});
            skLineSegment(sketch, "E815", {"start": v(-63.66, 28.56) * mm, "end": v(-63.66, 28.5) * mm});
            skLineSegment(sketch, "E816", {"start": v(-63.66, 28.5) * mm, "end": v(-63.66, 28.45) * mm});
            skLineSegment(sketch, "E817", {"start": v(-63.66, 28.45) * mm, "end": v(-63.65, 28.4) * mm});
            skLineSegment(sketch, "E818", {"start": v(-63.65, 28.4) * mm, "end": v(-63.65, 28.34) * mm});
            skLineSegment(sketch, "E819", {"start": v(-63.65, 28.34) * mm, "end": v(-63.64, 28.29) * mm});
            skLineSegment(sketch, "E820", {"start": v(-63.64, 28.29) * mm, "end": v(-63.63, 28.23) * mm});
            skLineSegment(sketch, "E821", {"start": v(-63.63, 28.23) * mm, "end": v(-63.61, 28.18) * mm});
            skLineSegment(sketch, "E822", {"start": v(-63.61, 28.18) * mm, "end": v(-63.6, 28.12) * mm});
            skLineSegment(sketch, "E823", {"start": v(-63.6, 28.12) * mm, "end": v(-63.58, 28.07) * mm});
            skLineSegment(sketch, "E824", {"start": v(-63.58, 28.07) * mm, "end": v(-63.56, 28.02) * mm});
            skLineSegment(sketch, "E825", {"start": v(-63.56, 28.02) * mm, "end": v(-63.54, 27.97) * mm});
            skLineSegment(sketch, "E826", {"start": v(-63.54, 27.97) * mm, "end": v(-63.52, 27.92) * mm});
            skLineSegment(sketch, "E827", {"start": v(-63.52, 27.92) * mm, "end": v(-63.5, 27.87) * mm});
            skLineSegment(sketch, "E828", {"start": v(-63.5, 27.87) * mm, "end": v(-63.47, 27.82) * mm});
            skLineSegment(sketch, "E829", {"start": v(-63.47, 27.82) * mm, "end": v(-63.44, 27.77) * mm});
            skLineSegment(sketch, "E830", {"start": v(-63.44, 27.77) * mm, "end": v(-63.41, 27.72) * mm});
            skLineSegment(sketch, "E831", {"start": v(-63.41, 27.72) * mm, "end": v(-63.38, 27.67) * mm});
            skLineSegment(sketch, "E832", {"start": v(-63.38, 27.67) * mm, "end": v(-63.35, 27.63) * mm});
            skLineSegment(sketch, "E833", {"start": v(-63.35, 27.63) * mm, "end": v(-63.32, 27.58) * mm});
            skLineSegment(sketch, "E834", {"start": v(-63.32, 27.58) * mm, "end": v(-63.28, 27.54) * mm});
            skLineSegment(sketch, "E835", {"start": v(-63.28, 27.54) * mm, "end": v(-63.24, 27.5) * mm});
            skLineSegment(sketch, "E836", {"start": v(-63.24, 27.5) * mm, "end": v(-63.2, 27.46) * mm});
            skLineSegment(sketch, "E837", {"start": v(-63.2, 27.46) * mm, "end": v(-63.17, 27.42) * mm});
            skLineSegment(sketch, "E838", {"start": v(-63.17, 27.42) * mm, "end": v(-63.13, 27.38) * mm});
            skLineSegment(sketch, "E839", {"start": v(-63.13, 27.38) * mm, "end": v(-63.08, 27.35) * mm});
            skLineSegment(sketch, "E840", {"start": v(-63.08, 27.35) * mm, "end": v(-63.04, 27.31) * mm});
            skLineSegment(sketch, "E841", {"start": v(-63.04, 27.31) * mm, "end": v(-63, 27.28) * mm});
            skLineSegment(sketch, "E842", {"start": v(-63, 27.28) * mm, "end": v(-62.95, 27.25) * mm});
            skLineSegment(sketch, "E843", {"start": v(-62.95, 27.25) * mm, "end": v(-62.9, 27.22) * mm});
            skLineSegment(sketch, "E844", {"start": v(-62.9, 27.22) * mm, "end": v(-62.85, 27.19) * mm});
            skLineSegment(sketch, "E845", {"start": v(-62.85, 27.19) * mm, "end": v(-62.8, 27.16) * mm});
            skLineSegment(sketch, "E846", {"start": v(-62.8, 27.16) * mm, "end": v(-62.76, 27.13) * mm});
            skLineSegment(sketch, "E847", {"start": v(-62.76, 27.13) * mm, "end": v(-62.7, 27.11) * mm});
            skLineSegment(sketch, "E848", {"start": v(-62.7, 27.11) * mm, "end": v(-62.65, 27.09) * mm});
            skLineSegment(sketch, "E849", {"start": v(-62.65, 27.09) * mm, "end": v(-62.6, 27.07) * mm});
            skLineSegment(sketch, "E850", {"start": v(-62.6, 27.07) * mm, "end": v(-62.55, 27.05) * mm});
            skLineSegment(sketch, "E851", {"start": v(-62.55, 27.05) * mm, "end": v(-62.5, 27.04) * mm});
            skLineSegment(sketch, "E852", {"start": v(-62.5, 27.04) * mm, "end": v(-62.44, 27.02) * mm});
            skLineSegment(sketch, "E853", {"start": v(-62.44, 27.02) * mm, "end": v(-62.39, 27) * mm});
            skLineSegment(sketch, "E854", {"start": v(-62.39, 27) * mm, "end": v(-62.33, 27) * mm});
            skLineSegment(sketch, "E855", {"start": v(-62.33, 27) * mm, "end": v(-62.28, 26.99) * mm});
            skLineSegment(sketch, "E856", {"start": v(-62.28, 26.99) * mm, "end": v(-62.22, 26.98) * mm});
            skLineSegment(sketch, "E857", {"start": v(-62.22, 26.98) * mm, "end": v(-62.17, 26.98) * mm});
            skLineSegment(sketch, "E858", {"start": v(-62.17, 26.98) * mm, "end": v(-62.11, 26.98) * mm});
            skLineSegment(sketch, "E859", {"start": v(-62.11, 26.98) * mm, "end": v(-62.06, 26.97) * mm});
            skLineSegment(sketch, "E860", {"start": v(-62.06, 26.97) * mm, "end": v(-62, 26.98) * mm});
            skLineSegment(sketch, "E861", {"start": v(-62, 26.98) * mm, "end": v(-61.94, 26.98) * mm});
            skLineSegment(sketch, "E862", {"start": v(-61.94, 26.98) * mm, "end": v(-61.89, 26.98) * mm});
            skLineSegment(sketch, "E863", {"start": v(-61.89, 26.98) * mm, "end": v(-61.83, 27) * mm});
            skLineSegment(sketch, "E864", {"start": v(-61.83, 27) * mm, "end": v(-61.78, 27) * mm});
            skLineSegment(sketch, "E865", {"start": v(-61.78, 27) * mm, "end": v(-61.72, 27) * mm});
            skLineSegment(sketch, "E866", {"start": v(-61.72, 27) * mm, "end": v(-61.67, 27.02) * mm});
            skLineSegment(sketch, "E867", {"start": v(-61.67, 27.02) * mm, "end": v(-61.61, 27.04) * mm});
            skLineSegment(sketch, "E868", {"start": v(-61.61, 27.04) * mm, "end": v(-61.56, 27.05) * mm});
            skLineSegment(sketch, "E869", {"start": v(-61.56, 27.05) * mm, "end": v(-61.5, 27.07) * mm});
            skLineSegment(sketch, "E870", {"start": v(-61.5, 27.07) * mm, "end": v(-61.45, 27.1) * mm});
            skLineSegment(sketch, "E871", {"start": v(-61.45, 27.1) * mm, "end": v(-61.4, 27.11) * mm});
            skLineSegment(sketch, "E872", {"start": v(-61.4, 27.11) * mm, "end": v(-61.35, 27.14) * mm});
            skLineSegment(sketch, "E873", {"start": v(-61.35, 27.14) * mm, "end": v(-61.3, 27.16) * mm});
            skLineSegment(sketch, "E874", {"start": v(-61.3, 27.16) * mm, "end": v(-61.25, 27.19) * mm});
            skLineSegment(sketch, "E875", {"start": v(-61.25, 27.19) * mm, "end": v(-61.2, 27.22) * mm});
            skLineSegment(sketch, "E876", {"start": v(-61.2, 27.22) * mm, "end": v(-61.16, 27.25) * mm});
            skLineSegment(sketch, "E877", {"start": v(-61.16, 27.25) * mm, "end": v(-61.11, 27.28) * mm});
            skLineSegment(sketch, "E878", {"start": v(-61.11, 27.28) * mm, "end": v(-61.07, 27.32) * mm});
            skLineSegment(sketch, "E879", {"start": v(-61.07, 27.32) * mm, "end": v(-61.02, 27.35) * mm});
            skLineSegment(sketch, "E880", {"start": v(-61.02, 27.35) * mm, "end": v(-60.98, 27.39) * mm});
            skLineSegment(sketch, "E881", {"start": v(-60.98, 27.39) * mm, "end": v(-60.94, 27.43) * mm});
            skLineSegment(sketch, "E882", {"start": v(-60.94, 27.43) * mm, "end": v(-60.9, 27.47) * mm});
            skLineSegment(sketch, "E883", {"start": v(-60.9, 27.47) * mm, "end": v(-60.86, 27.5) * mm});
            skLineSegment(sketch, "E884", {"start": v(-60.86, 27.5) * mm, "end": v(-60.82, 27.55) * mm});
            skLineSegment(sketch, "E885", {"start": v(-60.82, 27.55) * mm, "end": v(-60.79, 27.6) * mm});
            skLineSegment(sketch, "E886", {"start": v(-60.79, 27.6) * mm, "end": v(-60.76, 27.64) * mm});
            skLineSegment(sketch, "E887", {"start": v(-60.76, 27.64) * mm, "end": v(-60.72, 27.68) * mm});
            skLineSegment(sketch, "E888", {"start": v(-60.72, 27.68) * mm, "end": v(-60.7, 27.73) * mm});
            skLineSegment(sketch, "E889", {"start": v(-60.7, 27.73) * mm, "end": v(-60.66, 27.78) * mm});
            skLineSegment(sketch, "E890", {"start": v(-60.66, 27.78) * mm, "end": v(-60.64, 27.83) * mm});
            skLineSegment(sketch, "E891", {"start": v(-60.64, 27.83) * mm, "end": v(-60.61, 27.88) * mm});
            skLineSegment(sketch, "E892", {"start": v(-60.61, 27.88) * mm, "end": v(-60.59, 27.93) * mm});
            skLineSegment(sketch, "E893", {"start": v(-60.59, 27.93) * mm, "end": v(-60.57, 27.98) * mm});
            skLineSegment(sketch, "E894", {"start": v(-60.57, 27.98) * mm, "end": v(-60.54, 28.03) * mm});
            skLineSegment(sketch, "E895", {"start": v(-60.54, 28.03) * mm, "end": v(-60.53, 28.09) * mm});
            skLineSegment(sketch, "E896", {"start": v(-60.53, 28.09) * mm, "end": v(-60.51, 28.14) * mm});
            skLineSegment(sketch, "E897", {"start": v(-60.51, 28.14) * mm, "end": v(-60.5, 28.2) * mm});
            skLineSegment(sketch, "E898", {"start": v(-60.5, 28.2) * mm, "end": v(-60.48, 28.25) * mm});
            skLineSegment(sketch, "E899", {"start": v(-60.48, 28.25) * mm, "end": v(-60.47, 28.3) * mm});
            skLineSegment(sketch, "E900", {"start": v(-60.47, 28.3) * mm, "end": v(-60.46, 28.36) * mm});
            skLineSegment(sketch, "E901", {"start": v(-60.46, 28.36) * mm, "end": v(-60.46, 28.41) * mm});
            skLineSegment(sketch, "E902", {"start": v(-60.46, 28.41) * mm, "end": v(-60.45, 28.47) * mm});
            skLineSegment(sketch, "E903", {"start": v(-60.45, 28.47) * mm, "end": v(-60.45, 28.53) * mm});
            skLineSegment(sketch, "E904", {"start": v(-60.45, 28.53) * mm, "end": v(-60.45, 28.58) * mm});
            skLineSegment(sketch, "E905", {"start": v(19.15, 31.12) * mm, "end": v(21.7, 28.58) * mm});
            skLineSegment(sketch, "E906", {"start": v(21.7, 28.58) * mm, "end": v(21.7, 18.43) * mm});
            skLineSegment(sketch, "E907", {"start": v(21.7, 18.43) * mm, "end": v(24.23, 15.89) * mm});
            skLineSegment(sketch, "E908", {"start": v(24.23, 15.89) * mm, "end": v(24.23, -18.37) * mm});
            skLineSegment(sketch, "E909", {"start": v(24.23, -18.37) * mm, "end": v(21.7, -20.9) * mm});
            skLineSegment(sketch, "E910", {"start": v(21.7, -20.9) * mm, "end": v(21.7, -21.18) * mm});
            skLineSegment(sketch, "E911", {"start": v(21.7, -21.18) * mm, "end": v(21.67, -21.44) * mm});
            skLineSegment(sketch, "E912", {"start": v(21.67, -21.44) * mm, "end": v(21.57, -21.67) * mm});
            skLineSegment(sketch, "E913", {"start": v(21.57, -21.67) * mm, "end": v(21.42, -21.88) * mm});
            skLineSegment(sketch, "E914", {"start": v(21.42, -21.88) * mm, "end": v(21.2, -22.05) * mm});
            skLineSegment(sketch, "E915", {"start": v(21.2, -22.05) * mm, "end": v(20.95, -22.14) * mm});
            skLineSegment(sketch, "E916", {"start": v(20.95, -22.14) * mm, "end": v(20.7, -22.18) * mm});
            skLineSegment(sketch, "E917", {"start": v(20.7, -22.18) * mm, "end": v(-76.3, -22.18) * mm});
            skLineSegment(sketch, "E918", {"start": v(-76.3, -22.18) * mm, "end": v(-76.55, -22.14) * mm});
            skLineSegment(sketch, "E919", {"start": v(-76.55, -22.14) * mm, "end": v(-76.78, -22.05) * mm});
            skLineSegment(sketch, "E920", {"start": v(-76.78, -22.05) * mm, "end": v(-77, -21.88) * mm});
            skLineSegment(sketch, "E921", {"start": v(-77, -21.88) * mm, "end": v(-77.16, -21.67) * mm});
            skLineSegment(sketch, "E922", {"start": v(-77.16, -21.67) * mm, "end": v(-77.25, -21.44) * mm});
            skLineSegment(sketch, "E923", {"start": v(-77.25, -21.44) * mm, "end": v(-77.3, -21.18) * mm});
            skLineSegment(sketch, "E924", {"start": v(-77.3, -21.18) * mm, "end": v(-77.3, 30.1) * mm});
            skLineSegment(sketch, "E925", {"start": v(-77.3, 30.1) * mm, "end": v(-77.25, 30.38) * mm});
            skLineSegment(sketch, "E926", {"start": v(-77.25, 30.38) * mm, "end": v(-77.16, 30.61) * mm});
            skLineSegment(sketch, "E927", {"start": v(-77.16, 30.61) * mm, "end": v(-77, 30.83) * mm});
            skLineSegment(sketch, "E928", {"start": v(-77, 30.83) * mm, "end": v(-76.78, 30.97) * mm});
            skLineSegment(sketch, "E929", {"start": v(-76.78, 30.97) * mm, "end": v(-76.55, 31.08) * mm});
            skLineSegment(sketch, "E930", {"start": v(-76.55, 31.08) * mm, "end": v(-76.3, 31.12) * mm});
            skLineSegment(sketch, "E931", {"start": v(-76.3, 31.12) * mm, "end": v(19.15, 31.12) * mm});
            skLineSegment(sketch, "E932", {"start": v(-9.69, -14.56) * mm, "end": v(-9.69, -14.5) * mm});
            skLineSegment(sketch, "E933", {"start": v(-9.69, -14.5) * mm, "end": v(-9.7, -14.45) * mm});
            skLineSegment(sketch, "E934", {"start": v(-9.7, -14.45) * mm, "end": v(-9.7, -14.4) * mm});
            skLineSegment(sketch, "E935", {"start": v(-9.7, -14.4) * mm, "end": v(-9.7, -14.34) * mm});
            skLineSegment(sketch, "E936", {"start": v(-9.7, -14.34) * mm, "end": v(-9.71, -14.28) * mm});
            skLineSegment(sketch, "E937", {"start": v(-9.71, -14.28) * mm, "end": v(-9.72, -14.23) * mm});
            skLineSegment(sketch, "E938", {"start": v(-9.72, -14.23) * mm, "end": v(-9.73, -14.17) * mm});
            skLineSegment(sketch, "E939", {"start": v(-9.73, -14.17) * mm, "end": v(-9.75, -14.12) * mm});
            skLineSegment(sketch, "E940", {"start": v(-9.75, -14.12) * mm, "end": v(-9.76, -14.07) * mm});
            skLineSegment(sketch, "E941", {"start": v(-9.76, -14.07) * mm, "end": v(-9.78, -14.01) * mm});
            skLineSegment(sketch, "E942", {"start": v(-9.78, -14.01) * mm, "end": v(-9.8, -13.96) * mm});
            skLineSegment(sketch, "E943", {"start": v(-9.8, -13.96) * mm, "end": v(-9.82, -13.91) * mm});
            skLineSegment(sketch, "E944", {"start": v(-9.82, -13.91) * mm, "end": v(-9.85, -13.86) * mm});
            skLineSegment(sketch, "E945", {"start": v(-9.85, -13.86) * mm, "end": v(-9.87, -13.81) * mm});
            skLineSegment(sketch, "E946", {"start": v(-9.87, -13.81) * mm, "end": v(-9.9, -13.76) * mm});
            skLineSegment(sketch, "E947", {"start": v(-9.9, -13.76) * mm, "end": v(-9.93, -13.71) * mm});
            skLineSegment(sketch, "E948", {"start": v(-9.93, -13.71) * mm, "end": v(-9.96, -13.67) * mm});
            skLineSegment(sketch, "E949", {"start": v(-9.96, -13.67) * mm, "end": v(-9.99, -13.62) * mm});
            skLineSegment(sketch, "E950", {"start": v(-9.99, -13.62) * mm, "end": v(-10.02, -13.58) * mm});
            skLineSegment(sketch, "E951", {"start": v(-10.02, -13.58) * mm, "end": v(-10.06, -13.53) * mm});
            skLineSegment(sketch, "E952", {"start": v(-10.06, -13.53) * mm, "end": v(-10.1, -13.5) * mm});
            skLineSegment(sketch, "E953", {"start": v(-10.1, -13.5) * mm, "end": v(-10.13, -13.45) * mm});
            skLineSegment(sketch, "E954", {"start": v(-10.13, -13.45) * mm, "end": v(-10.17, -13.41) * mm});
            skLineSegment(sketch, "E955", {"start": v(-10.17, -13.41) * mm, "end": v(-10.21, -13.37) * mm});
            skLineSegment(sketch, "E956", {"start": v(-10.21, -13.37) * mm, "end": v(-10.25, -13.34) * mm});
            skLineSegment(sketch, "E957", {"start": v(-10.25, -13.34) * mm, "end": v(-10.3, -13.3) * mm});
            skLineSegment(sketch, "E958", {"start": v(-10.3, -13.3) * mm, "end": v(-10.34, -13.27) * mm});
            skLineSegment(sketch, "E959", {"start": v(-10.34, -13.27) * mm, "end": v(-10.39, -13.23) * mm});
            skLineSegment(sketch, "E960", {"start": v(-10.39, -13.23) * mm, "end": v(-10.43, -13.2) * mm});
            skLineSegment(sketch, "E961", {"start": v(-10.43, -13.2) * mm, "end": v(-10.48, -13.17) * mm});
            skLineSegment(sketch, "E962", {"start": v(-10.48, -13.17) * mm, "end": v(-10.53, -13.15) * mm});
            skLineSegment(sketch, "E963", {"start": v(-10.53, -13.15) * mm, "end": v(-10.58, -13.12) * mm});
            skLineSegment(sketch, "E964", {"start": v(-10.58, -13.12) * mm, "end": v(-10.63, -13.1) * mm});
            skLineSegment(sketch, "E965", {"start": v(-10.63, -13.1) * mm, "end": v(-10.68, -13.08) * mm});
            skLineSegment(sketch, "E966", {"start": v(-10.68, -13.08) * mm, "end": v(-10.73, -13.05) * mm});
            skLineSegment(sketch, "E967", {"start": v(-10.73, -13.05) * mm, "end": v(-10.78, -13.04) * mm});
            skLineSegment(sketch, "E968", {"start": v(-10.78, -13.04) * mm, "end": v(-10.84, -13.02) * mm});
            skLineSegment(sketch, "E969", {"start": v(-10.84, -13.02) * mm, "end": v(-10.9, -13) * mm});
            skLineSegment(sketch, "E970", {"start": v(-10.9, -13) * mm, "end": v(-10.95, -13) * mm});
            skLineSegment(sketch, "E971", {"start": v(-10.95, -13) * mm, "end": v(-11, -12.98) * mm});
            skLineSegment(sketch, "E972", {"start": v(-11, -12.98) * mm, "end": v(-11.05, -12.97) * mm});
            skLineSegment(sketch, "E973", {"start": v(-11.05, -12.97) * mm, "end": v(-11.1, -12.96) * mm});
            skLineSegment(sketch, "E974", {"start": v(-11.1, -12.96) * mm, "end": v(-11.17, -12.96) * mm});
            skLineSegment(sketch, "E975", {"start": v(-11.17, -12.96) * mm, "end": v(-11.22, -12.95) * mm});
            skLineSegment(sketch, "E976", {"start": v(-11.22, -12.95) * mm, "end": v(-11.28, -12.95) * mm});
            skLineSegment(sketch, "E977", {"start": v(-11.28, -12.95) * mm, "end": v(-11.33, -12.95) * mm});
            skLineSegment(sketch, "E978", {"start": v(-11.33, -12.95) * mm, "end": v(-11.39, -12.96) * mm});
            skLineSegment(sketch, "E979", {"start": v(-11.39, -12.96) * mm, "end": v(-11.44, -12.96) * mm});
            skLineSegment(sketch, "E980", {"start": v(-11.44, -12.96) * mm, "end": v(-11.5, -12.97) * mm});
            skLineSegment(sketch, "E981", {"start": v(-11.5, -12.97) * mm, "end": v(-11.55, -12.97) * mm});
            skLineSegment(sketch, "E982", {"start": v(-11.55, -12.97) * mm, "end": v(-11.6, -12.98) * mm});
            skLineSegment(sketch, "E983", {"start": v(-11.6, -12.98) * mm, "end": v(-11.66, -13) * mm});
            skLineSegment(sketch, "E984", {"start": v(-11.66, -13) * mm, "end": v(-11.72, -13) * mm});
            skLineSegment(sketch, "E985", {"start": v(-11.72, -13) * mm, "end": v(-11.77, -13.02) * mm});
            skLineSegment(sketch, "E986", {"start": v(-11.77, -13.02) * mm, "end": v(-11.82, -13.04) * mm});
            skLineSegment(sketch, "E987", {"start": v(-11.82, -13.04) * mm, "end": v(-11.88, -13.06) * mm});
            skLineSegment(sketch, "E988", {"start": v(-11.88, -13.06) * mm, "end": v(-11.93, -13.08) * mm});
            skLineSegment(sketch, "E989", {"start": v(-11.93, -13.08) * mm, "end": v(-11.98, -13.1) * mm});
            skLineSegment(sketch, "E990", {"start": v(-11.98, -13.1) * mm, "end": v(-12.03, -13.13) * mm});
            skLineSegment(sketch, "E991", {"start": v(-12.03, -13.13) * mm, "end": v(-12.08, -13.16) * mm});
            skLineSegment(sketch, "E992", {"start": v(-12.08, -13.16) * mm, "end": v(-12.13, -13.18) * mm});
            skLineSegment(sketch, "E993", {"start": v(-12.13, -13.18) * mm, "end": v(-12.17, -13.21) * mm});
            skLineSegment(sketch, "E994", {"start": v(-12.17, -13.21) * mm, "end": v(-12.22, -13.24) * mm});
            skLineSegment(sketch, "E995", {"start": v(-12.22, -13.24) * mm, "end": v(-12.26, -13.28) * mm});
            skLineSegment(sketch, "E996", {"start": v(-12.26, -13.28) * mm, "end": v(-12.3, -13.31) * mm});
            skLineSegment(sketch, "E997", {"start": v(-12.3, -13.31) * mm, "end": v(-12.35, -13.35) * mm});
            skLineSegment(sketch, "E998", {"start": v(-12.35, -13.35) * mm, "end": v(-12.4, -13.39) * mm});
            skLineSegment(sketch, "E999", {"start": v(-12.4, -13.39) * mm, "end": v(-12.43, -13.42) * mm});
            skLineSegment(sketch, "E1000", {"start": v(-12.43, -13.42) * mm, "end": v(-12.47, -13.46) * mm});
            skLineSegment(sketch, "E1001", {"start": v(-12.47, -13.46) * mm, "end": v(-12.5, -13.5) * mm});
            skLineSegment(sketch, "E1002", {"start": v(-12.5, -13.5) * mm, "end": v(-12.54, -13.55) * mm});
            skLineSegment(sketch, "E1003", {"start": v(-12.54, -13.55) * mm, "end": v(-12.58, -13.6) * mm});
            skLineSegment(sketch, "E1004", {"start": v(-12.58, -13.6) * mm, "end": v(-12.61, -13.64) * mm});
            skLineSegment(sketch, "E1005", {"start": v(-12.61, -13.64) * mm, "end": v(-12.64, -13.68) * mm});
            skLineSegment(sketch, "E1006", {"start": v(-12.64, -13.68) * mm, "end": v(-12.67, -13.73) * mm});
            skLineSegment(sketch, "E1007", {"start": v(-12.67, -13.73) * mm, "end": v(-12.7, -13.78) * mm});
            skLineSegment(sketch, "E1008", {"start": v(-12.7, -13.78) * mm, "end": v(-12.73, -13.83) * mm});
            skLineSegment(sketch, "E1009", {"start": v(-12.73, -13.83) * mm, "end": v(-12.75, -13.88) * mm});
            skLineSegment(sketch, "E1010", {"start": v(-12.75, -13.88) * mm, "end": v(-12.77, -13.93) * mm});
            skLineSegment(sketch, "E1011", {"start": v(-12.77, -13.93) * mm, "end": v(-12.8, -13.98) * mm});
            skLineSegment(sketch, "E1012", {"start": v(-12.8, -13.98) * mm, "end": v(-12.81, -14.03) * mm});
            skLineSegment(sketch, "E1013", {"start": v(-12.81, -14.03) * mm, "end": v(-12.83, -14.09) * mm});
            skLineSegment(sketch, "E1014", {"start": v(-12.83, -14.09) * mm, "end": v(-12.85, -14.14) * mm});
            skLineSegment(sketch, "E1015", {"start": v(-12.85, -14.14) * mm, "end": v(-12.86, -14.2) * mm});
            skLineSegment(sketch, "E1016", {"start": v(-12.86, -14.2) * mm, "end": v(-12.87, -14.25) * mm});
            skLineSegment(sketch, "E1017", {"start": v(-12.87, -14.25) * mm, "end": v(-12.88, -14.3) * mm});
            skLineSegment(sketch, "E1018", {"start": v(-12.88, -14.3) * mm, "end": v(-12.9, -14.36) * mm});
            skLineSegment(sketch, "E1019", {"start": v(-12.9, -14.36) * mm, "end": v(-12.9, -14.41) * mm});
            skLineSegment(sketch, "E1020", {"start": v(-12.9, -14.41) * mm, "end": v(-12.9, -14.47) * mm});
            skLineSegment(sketch, "E1021", {"start": v(-12.9, -14.47) * mm, "end": v(-12.9, -14.52) * mm});
            skLineSegment(sketch, "E1022", {"start": v(-12.9, -14.52) * mm, "end": v(-12.9, -14.58) * mm});
            skLineSegment(sketch, "E1023", {"start": v(-12.9, -14.58) * mm, "end": v(-12.9, -14.64) * mm});
            skLineSegment(sketch, "E1024", {"start": v(-12.9, -14.64) * mm, "end": v(-12.9, -14.7) * mm});
            skLineSegment(sketch, "E1025", {"start": v(-12.9, -14.7) * mm, "end": v(-12.9, -14.75) * mm});
            skLineSegment(sketch, "E1026", {"start": v(-12.9, -14.75) * mm, "end": v(-12.89, -14.8) * mm});
            skLineSegment(sketch, "E1027", {"start": v(-12.89, -14.8) * mm, "end": v(-12.88, -14.86) * mm});
            skLineSegment(sketch, "E1028", {"start": v(-12.88, -14.86) * mm, "end": v(-12.86, -14.91) * mm});
            skLineSegment(sketch, "E1029", {"start": v(-12.86, -14.91) * mm, "end": v(-12.85, -14.97) * mm});
            skLineSegment(sketch, "E1030", {"start": v(-12.85, -14.97) * mm, "end": v(-12.84, -15.02) * mm});
            skLineSegment(sketch, "E1031", {"start": v(-12.84, -15.02) * mm, "end": v(-12.82, -15.07) * mm});
            skLineSegment(sketch, "E1032", {"start": v(-12.82, -15.07) * mm, "end": v(-12.8, -15.12) * mm});
            skLineSegment(sketch, "E1033", {"start": v(-12.8, -15.12) * mm, "end": v(-12.78, -15.18) * mm});
            skLineSegment(sketch, "E1034", {"start": v(-12.78, -15.18) * mm, "end": v(-12.76, -15.23) * mm});
            skLineSegment(sketch, "E1035", {"start": v(-12.76, -15.23) * mm, "end": v(-12.73, -15.28) * mm});
            skLineSegment(sketch, "E1036", {"start": v(-12.73, -15.28) * mm, "end": v(-12.7, -15.33) * mm});
            skLineSegment(sketch, "E1037", {"start": v(-12.7, -15.33) * mm, "end": v(-12.68, -15.38) * mm});
            skLineSegment(sketch, "E1038", {"start": v(-12.68, -15.38) * mm, "end": v(-12.65, -15.42) * mm});
            skLineSegment(sketch, "E1039", {"start": v(-12.65, -15.42) * mm, "end": v(-12.62, -15.47) * mm});
            skLineSegment(sketch, "E1040", {"start": v(-12.62, -15.47) * mm, "end": v(-12.59, -15.52) * mm});
            skLineSegment(sketch, "E1041", {"start": v(-12.59, -15.52) * mm, "end": v(-12.56, -15.56) * mm});
            skLineSegment(sketch, "E1042", {"start": v(-12.56, -15.56) * mm, "end": v(-12.52, -15.6) * mm});
            skLineSegment(sketch, "E1043", {"start": v(-12.52, -15.6) * mm, "end": v(-12.48, -15.64) * mm});
            skLineSegment(sketch, "E1044", {"start": v(-12.48, -15.64) * mm, "end": v(-12.45, -15.68) * mm});
            skLineSegment(sketch, "E1045", {"start": v(-12.45, -15.68) * mm, "end": v(-12.4, -15.72) * mm});
            skLineSegment(sketch, "E1046", {"start": v(-12.4, -15.72) * mm, "end": v(-12.36, -15.76) * mm});
            skLineSegment(sketch, "E1047", {"start": v(-12.36, -15.76) * mm, "end": v(-12.32, -15.8) * mm});
            skLineSegment(sketch, "E1048", {"start": v(-12.32, -15.8) * mm, "end": v(-12.28, -15.83) * mm});
            skLineSegment(sketch, "E1049", {"start": v(-12.28, -15.83) * mm, "end": v(-12.23, -15.87) * mm});
            skLineSegment(sketch, "E1050", {"start": v(-12.23, -15.87) * mm, "end": v(-12.19, -15.9) * mm});
            skLineSegment(sketch, "E1051", {"start": v(-12.19, -15.9) * mm, "end": v(-12.14, -15.93) * mm});
            skLineSegment(sketch, "E1052", {"start": v(-12.14, -15.93) * mm, "end": v(-12.1, -15.96) * mm});
            skLineSegment(sketch, "E1053", {"start": v(-12.1, -15.96) * mm, "end": v(-12.05, -15.98) * mm});
            skLineSegment(sketch, "E1054", {"start": v(-12.05, -15.98) * mm, "end": v(-12, -16) * mm});
            skLineSegment(sketch, "E1055", {"start": v(-12, -16) * mm, "end": v(-11.94, -16.03) * mm});
            skLineSegment(sketch, "E1056", {"start": v(-11.94, -16.03) * mm, "end": v(-11.9, -16.05) * mm});
            skLineSegment(sketch, "E1057", {"start": v(-11.9, -16.05) * mm, "end": v(-11.84, -16.07) * mm});
            skLineSegment(sketch, "E1058", {"start": v(-11.84, -16.07) * mm, "end": v(-11.79, -16.1) * mm});
            skLineSegment(sketch, "E1059", {"start": v(-11.79, -16.1) * mm, "end": v(-11.74, -16.1) * mm});
            skLineSegment(sketch, "E1060", {"start": v(-11.74, -16.1) * mm, "end": v(-11.68, -16.12) * mm});
            skLineSegment(sketch, "E1061", {"start": v(-11.68, -16.12) * mm, "end": v(-11.63, -16.13) * mm});
            skLineSegment(sketch, "E1062", {"start": v(-11.63, -16.13) * mm, "end": v(-11.57, -16.14) * mm});
            skLineSegment(sketch, "E1063", {"start": v(-11.57, -16.14) * mm, "end": v(-11.52, -16.15) * mm});
            skLineSegment(sketch, "E1064", {"start": v(-11.52, -16.15) * mm, "end": v(-11.46, -16.16) * mm});
            skLineSegment(sketch, "E1065", {"start": v(-11.46, -16.16) * mm, "end": v(-11.4, -16.17) * mm});
            skLineSegment(sketch, "E1066", {"start": v(-11.4, -16.17) * mm, "end": v(-11.35, -16.17) * mm});
            skLineSegment(sketch, "E1067", {"start": v(-11.35, -16.17) * mm, "end": v(-11.3, -16.17) * mm});
            skLineSegment(sketch, "E1068", {"start": v(-11.3, -16.17) * mm, "end": v(-11.24, -16.17) * mm});
            skLineSegment(sketch, "E1069", {"start": v(-11.24, -16.17) * mm, "end": v(-11.18, -16.17) * mm});
            skLineSegment(sketch, "E1070", {"start": v(-11.18, -16.17) * mm, "end": v(-11.13, -16.16) * mm});
            skLineSegment(sketch, "E1071", {"start": v(-11.13, -16.16) * mm, "end": v(-11.07, -16.15) * mm});
            skLineSegment(sketch, "E1072", {"start": v(-11.07, -16.15) * mm, "end": v(-11.02, -16.14) * mm});
            skLineSegment(sketch, "E1073", {"start": v(-11.02, -16.14) * mm, "end": v(-10.96, -16.13) * mm});
            skLineSegment(sketch, "E1074", {"start": v(-10.96, -16.13) * mm, "end": v(-10.9, -16.12) * mm});
            skLineSegment(sketch, "E1075", {"start": v(-10.9, -16.12) * mm, "end": v(-10.85, -16.1) * mm});
            skLineSegment(sketch, "E1076", {"start": v(-10.85, -16.1) * mm, "end": v(-10.8, -16.1) * mm});
            skLineSegment(sketch, "E1077", {"start": v(-10.8, -16.1) * mm, "end": v(-10.75, -16.07) * mm});
            skLineSegment(sketch, "E1078", {"start": v(-10.75, -16.07) * mm, "end": v(-10.7, -16.05) * mm});
            skLineSegment(sketch, "E1079", {"start": v(-10.7, -16.05) * mm, "end": v(-10.64, -16.03) * mm});
            skLineSegment(sketch, "E1080", {"start": v(-10.64, -16.03) * mm, "end": v(-10.6, -16) * mm});
            skLineSegment(sketch, "E1081", {"start": v(-10.6, -16) * mm, "end": v(-10.54, -15.98) * mm});
            skLineSegment(sketch, "E1082", {"start": v(-10.54, -15.98) * mm, "end": v(-10.5, -15.95) * mm});
            skLineSegment(sketch, "E1083", {"start": v(-10.5, -15.95) * mm, "end": v(-10.44, -15.92) * mm});
            skLineSegment(sketch, "E1084", {"start": v(-10.44, -15.92) * mm, "end": v(-10.4, -15.9) * mm});
            skLineSegment(sketch, "E1085", {"start": v(-10.4, -15.9) * mm, "end": v(-10.35, -15.86) * mm});
            skLineSegment(sketch, "E1086", {"start": v(-10.35, -15.86) * mm, "end": v(-10.3, -15.83) * mm});
            skLineSegment(sketch, "E1087", {"start": v(-10.3, -15.83) * mm, "end": v(-10.26, -15.8) * mm});
            skLineSegment(sketch, "E1088", {"start": v(-10.26, -15.8) * mm, "end": v(-10.22, -15.76) * mm});
            skLineSegment(sketch, "E1089", {"start": v(-10.22, -15.76) * mm, "end": v(-10.18, -15.72) * mm});
            skLineSegment(sketch, "E1090", {"start": v(-10.18, -15.72) * mm, "end": v(-10.14, -15.68) * mm});
            skLineSegment(sketch, "E1091", {"start": v(-10.14, -15.68) * mm, "end": v(-10.1, -15.64) * mm});
            skLineSegment(sketch, "E1092", {"start": v(-10.1, -15.64) * mm, "end": v(-10.06, -15.6) * mm});
            skLineSegment(sketch, "E1093", {"start": v(-10.06, -15.6) * mm, "end": v(-10.03, -15.55) * mm});
            skLineSegment(sketch, "E1094", {"start": v(-10.03, -15.55) * mm, "end": v(-10, -15.5) * mm});
            skLineSegment(sketch, "E1095", {"start": v(-10, -15.5) * mm, "end": v(-9.96, -15.46) * mm});
            skLineSegment(sketch, "E1096", {"start": v(-9.96, -15.46) * mm, "end": v(-9.93, -15.41) * mm});
            skLineSegment(sketch, "E1097", {"start": v(-9.93, -15.41) * mm, "end": v(-9.9, -15.37) * mm});
            skLineSegment(sketch, "E1098", {"start": v(-9.9, -15.37) * mm, "end": v(-9.88, -15.32) * mm});
            skLineSegment(sketch, "E1099", {"start": v(-9.88, -15.32) * mm, "end": v(-9.85, -15.27) * mm});
            skLineSegment(sketch, "E1100", {"start": v(-9.85, -15.27) * mm, "end": v(-9.83, -15.22) * mm});
            skLineSegment(sketch, "E1101", {"start": v(-9.83, -15.22) * mm, "end": v(-9.8, -15.16) * mm});
            skLineSegment(sketch, "E1102", {"start": v(-9.8, -15.16) * mm, "end": v(-9.78, -15.11) * mm});
            skLineSegment(sketch, "E1103", {"start": v(-9.78, -15.11) * mm, "end": v(-9.77, -15.06) * mm});
            skLineSegment(sketch, "E1104", {"start": v(-9.77, -15.06) * mm, "end": v(-9.75, -15) * mm});
            skLineSegment(sketch, "E1105", {"start": v(-9.75, -15) * mm, "end": v(-9.73, -14.95) * mm});
            skLineSegment(sketch, "E1106", {"start": v(-9.73, -14.95) * mm, "end": v(-9.72, -14.9) * mm});
            skLineSegment(sketch, "E1107", {"start": v(-9.72, -14.9) * mm, "end": v(-9.71, -14.84) * mm});
            skLineSegment(sketch, "E1108", {"start": v(-9.71, -14.84) * mm, "end": v(-9.7, -14.78) * mm});
            skLineSegment(sketch, "E1109", {"start": v(-9.7, -14.78) * mm, "end": v(-9.7, -14.73) * mm});
            skLineSegment(sketch, "E1110", {"start": v(-9.7, -14.73) * mm, "end": v(-9.7, -14.67) * mm});
            skLineSegment(sketch, "E1111", {"start": v(-9.7, -14.67) * mm, "end": v(-9.69, -14.62) * mm});
            skLineSegment(sketch, "E1112", {"start": v(-9.69, -14.62) * mm, "end": v(-9.69, -14.56) * mm});
            skSolve(sketch);
        }
        {
            var Q0;
            Q0=qCreatedBy(makeId("Top.planeOp"),FACE);
            var sketch = newSketch(context, id + "F1", { "sketchPlane" : qUnion([Q0])});
            skPoint(sketch, "E1113", {"position": v(19.08, 31.4) * mm});
            skPoint(sketch, "E1114", {"position": v(21.62, 28.85) * mm});
            skPoint(sketch, "E1115", {"position": v(21.47, 18.66) * mm});
            skPoint(sketch, "E1116", {"position": v(24.17, 16.11) * mm});
            skPoint(sketch, "E1117", {"position": v(24.17, -18.11) * mm});
            skPoint(sketch, "E1118", {"position": v(21.65, -20.9) * mm});
            skPoint(sketch, "E1119", {"position": v(20.7, -22.17) * mm});
            skPoint(sketch, "E1120", {"position": v(21.65, -22.17) * mm});
            skPoint(sketch, "E1121", {"position": v(-76.3, -22.17) * mm});
            skPoint(sketch, "E1122", {"position": v(-77.29, -21.18) * mm});
            skPoint(sketch, "E1123", {"position": v(-77.29, -22.17) * mm});
            skPoint(sketch, "E1124", {"position": v(-77.29, 30.13) * mm});
            skPoint(sketch, "E1125", {"position": v(-76.29, 31.14) * mm});
            skPoint(sketch, "E1126", {"position": v(-77.29, 31.14) * mm});
            skLineSegment(sketch, "E1127", {"start": v(19.08, 31.4) * mm, "end": v(21.62, 28.85) * mm});
            skLineSegment(sketch, "E1128", {"start": v(21.47, 18.66) * mm, "end": v(24.17, 16.11) * mm});
            skLineSegment(sketch, "E1129", {"start": v(21.47, 18.66) * mm, "end": v(21.62, 28.85) * mm});
            skLineSegment(sketch, "E1130", {"start": v(24.17, 16.11) * mm, "end": v(24.17, -18.11) * mm});
            skLineSegment(sketch, "E1131", {"start": v(21.65, -22.17) * mm, "end": v(-76.3, -22.17) * mm});
            skLineSegment(sketch, "E1132", {"start": v(-77.29, -21.18) * mm, "end": v(-77.29, -22.17) * mm});
            skLineSegment(sketch, "E1133", {"start": v(-77.29, -22.17) * mm, "end": v(-76.3, -22.17) * mm});
            skLineSegment(sketch, "E1134", {"start": v(-77.29, -21.18) * mm, "end": v(-77.29, 30.13) * mm});
            skLineSegment(sketch, "E1135", {"start": v(-77.29, 31.14) * mm, "end": v(-77.29, 30.13) * mm});
            skLineSegment(sketch, "E1136", {"start": v(-76.29, 31.14) * mm, "end": v(-77.29, 31.14) * mm});
            skLineSegment(sketch, "E1137", {"start": v(-76.29, 31.14) * mm, "end": v(19.08, 31.4) * mm});
            skLineSegment(sketch, "E1138", {"start": v(24.17, -18.11) * mm, "end": v(21.65, -20.9) * mm});
            skLineSegment(sketch, "E1139", {"start": v(21.65, -20.9) * mm, "end": v(21.65, -22.17) * mm});
            skSolve(sketch);
        }
        {
            var Q0;
            Q0 = qSketchRegion(id + "F1", true);
            extrude(context, id + "F2", {"entities" : qUnion([Q0]), "depth" : 2 * mm});
        }
    });
